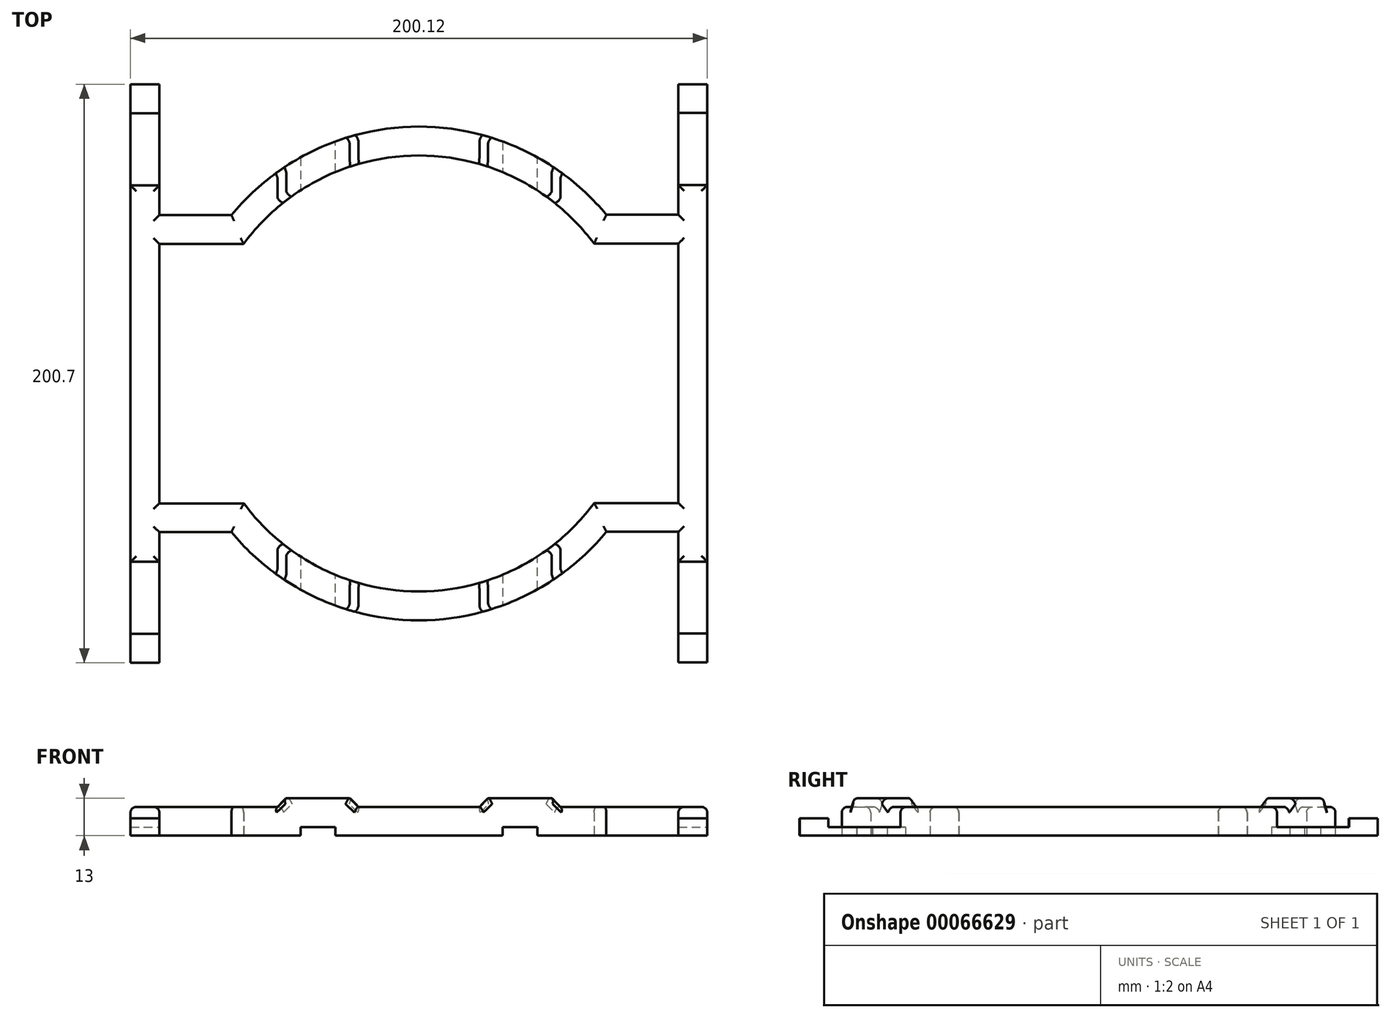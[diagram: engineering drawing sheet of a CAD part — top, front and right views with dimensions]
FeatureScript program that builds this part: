
annotation { "Feature Type Name" : "Feature", "Feature Type Description" : "" }
export const myFeature = defineFeature(function(context is Context, id is Id, definition is map)
    precondition{}
    {
        {
            var Q0;
            Q0=qCreatedBy(makeId("Top.planeOp"),FACE);
            var sketch = newSketch(context, id + "F0", { "sketchPlane" : qUnion([Q0])});
            skArc(sketch, "E0", {"start": v(-60.76, -45.05) * mm, "mid": v(0.06, -75.64) * mm, "end": v(60.83, -44.95) * mm});
            skLineSegment(sketch, "E1.bottom", {"start": v(-100.07, 100.25) * mm, "end": v(-90.07, 100.25) * mm});
            skLineSegment(sketch, "E1.top", {"start": v(-100.07, -100.35) * mm, "end": v(-90.07, -100.35) * mm});
            skLineSegment(sketch, "E2.bottom", {"start": v(90.05, 100.35) * mm, "end": v(100.05, 100.35) * mm});
            skLineSegment(sketch, "E2.top", {"start": v(90.05, -100.25) * mm, "end": v(100.05, -100.25) * mm});
            skLineSegment(sketch, "E3.bottom", {"start": v(-90.07, 54.95) * mm, "end": v(-65.07, 54.95) * mm});
            skLineSegment(sketch, "E4.bottom", {"start": v(-90.07, -55.05) * mm, "end": v(-65.07, -55.05) * mm});
            skLineSegment(sketch, "E5.bottom", {"start": v(90.05, 55.05) * mm, "end": v(65.05, 55.05) * mm});
            skLineSegment(sketch, "E6.top", {"start": v(90.05, -54.95) * mm, "end": v(65.05, -54.95) * mm});
            skLineSegment(sketch, "E7", {"start": v(-19, 83.46) * mm, "end": v(-19, 73.21) * mm});
            skLineSegment(sketch, "E8", {"start": v(-29, -80.52) * mm, "end": v(-29, -69.86) * mm});
            skLineSegment(sketch, "E9", {"start": v(19, 83.48) * mm, "end": v(19, 73.21) * mm});
            skLineSegment(sketch, "E10", {"start": v(41.12, -74.92) * mm, "end": v(41.12, -63.48) * mm});
            skLineSegment(sketch, "E11", {"start": v(-41.05, 74.96) * mm, "end": v(-41.05, 63.53) * mm});
            skLineSegment(sketch, "E12", {"start": v(-51.05, 68.42) * mm, "end": v(-51.05, 55.81) * mm});
            skLineSegment(sketch, "E13", {"start": v(51.12, -68.36) * mm, "end": v(51.12, -55.75) * mm});
            skLineSegment(sketch, "E14", {"start": v(29.07, 80.49) * mm, "end": v(29.07, 69.83) * mm});
            skLineSegment(sketch, "E15.trimOffspring", {"start": v(90.05, 45.05) * mm, "end": v(90.05, -44.95) * mm});
            skLineSegment(sketch, "E16.trimOffspring", {"start": v(-90.07, 44.95) * mm, "end": v(-90.07, -45.05) * mm});
            skLineSegment(sketch, "E17.trimOffspring", {"start": v(-51.05, -55.81) * mm, "end": v(-51.05, -68.48) * mm});
            skLineSegment(sketch, "E18.trimOffspring", {"start": v(-41.05, -63.53) * mm, "end": v(-41.05, -75) * mm});
            skLineSegment(sketch, "E19.trimOffspring", {"start": v(-29, 69.86) * mm, "end": v(-29, 80.48) * mm});
            skLineSegment(sketch, "E20.trimOffspring", {"start": v(-19, -73.21) * mm, "end": v(-19, -83.48) * mm});
            skLineSegment(sketch, "E21.trimOffspring", {"start": v(19, -73.21) * mm, "end": v(19, -83.46) * mm});
            skLineSegment(sketch, "E22.trimOffspring", {"start": v(29.07, -69.83) * mm, "end": v(29.07, -80.46) * mm});
            skLineSegment(sketch, "E23.trimOffspring", {"start": v(41.12, 63.48) * mm, "end": v(41.12, 74.96) * mm});
            skLineSegment(sketch, "E24.trimOffspring", {"start": v(51.12, 55.75) * mm, "end": v(51.12, 68.42) * mm});
            skArc(sketch, "E25.trimOffspring", {"start": v(-65.07, -55.05) * mm, "mid": v(0.02, -85.64) * mm, "end": v(65.05, -54.95) * mm});
            skArc(sketch, "E26.trimOffspring", {"start": v(65.05, 55.05) * mm, "mid": v(-0.03, 85.64) * mm, "end": v(-65.07, 54.95) * mm});
            skArc(sketch, "E27.trimOffspring", {"start": v(60.76, 45.05) * mm, "mid": v(-0.06, 75.64) * mm, "end": v(-60.83, 44.95) * mm});
            skLineSegment(sketch, "E28", {"start": v(-90.07, 44.95) * mm, "end": v(-60.83, 44.95) * mm});
            skLineSegment(sketch, "E29", {"start": v(-90.07, -45.05) * mm, "end": v(-60.76, -45.05) * mm});
            skLineSegment(sketch, "E30", {"start": v(60.83, -44.95) * mm, "end": v(90.05, -44.95) * mm});
            skLineSegment(sketch, "E31", {"start": v(90.05, 45.05) * mm, "end": v(60.76, 45.05) * mm});
            skLineSegment(sketch, "E32.bottom", {"start": v(-100.07, 65.25) * mm, "end": v(-90.07, 65.25) * mm});
            skLineSegment(sketch, "E32.top", {"start": v(-100.07, 90.25) * mm, "end": v(-90.07, 90.25) * mm});
            skLineSegment(sketch, "E32.left", {"start": v(-100.07, 65.25) * mm, "end": v(-100.07, 90.25) * mm});
            skLineSegment(sketch, "E33.bottom", {"start": v(-100.07, -90.35) * mm, "end": v(-90.07, -90.35) * mm});
            skLineSegment(sketch, "E33.top", {"start": v(-100.07, -65.35) * mm, "end": v(-90.07, -65.35) * mm});
            skLineSegment(sketch, "E33.left", {"start": v(-100.07, -90.35) * mm, "end": v(-100.07, -65.35) * mm});
            skLineSegment(sketch, "E33.right", {"start": v(-90.07, -90.35) * mm, "end": v(-90.07, -65.35) * mm});
            skLineSegment(sketch, "E34.bottom", {"start": v(90.05, -90.25) * mm, "end": v(100.05, -90.25) * mm});
            skLineSegment(sketch, "E34.top", {"start": v(90.05, -65.25) * mm, "end": v(100.05, -65.25) * mm});
            skLineSegment(sketch, "E34.left", {"start": v(90.05, -90.25) * mm, "end": v(90.05, -65.25) * mm});
            skLineSegment(sketch, "E34.right", {"start": v(100.05, -90.25) * mm, "end": v(100.05, -65.25) * mm});
            skLineSegment(sketch, "E35.bottom", {"start": v(90.05, 65.35) * mm, "end": v(100.05, 65.35) * mm});
            skLineSegment(sketch, "E35.top", {"start": v(90.05, 90.35) * mm, "end": v(100.05, 90.35) * mm});
            skLineSegment(sketch, "E35.left", {"start": v(90.05, 65.35) * mm, "end": v(90.05, 90.35) * mm});
            skLineSegment(sketch, "E35.right", {"start": v(100.05, 65.35) * mm, "end": v(100.05, 90.35) * mm});
            skLineSegment(sketch, "E36", {"start": v(-100.07, 90.25) * mm, "end": v(-100.07, 100.25) * mm});
            skLineSegment(sketch, "E37", {"start": v(-90.07, 100.25) * mm, "end": v(-90.07, 90.25) * mm});
            skLineSegment(sketch, "E38", {"start": v(-90.07, -65.35) * mm, "end": v(-90.07, -55.05) * mm});
            skLineSegment(sketch, "E39", {"start": v(-100.07, -65.35) * mm, "end": v(-100.07, 65.25) * mm});
            skLineSegment(sketch, "E40", {"start": v(-100.07, -90.35) * mm, "end": v(-100.07, -100.35) * mm});
            skLineSegment(sketch, "E41", {"start": v(-90.07, -100.35) * mm, "end": v(-90.07, -90.35) * mm});
            skLineSegment(sketch, "E42", {"start": v(90.05, -100.25) * mm, "end": v(90.05, -90.25) * mm});
            skLineSegment(sketch, "E43", {"start": v(90.05, -65.25) * mm, "end": v(90.05, -54.95) * mm});
            skLineSegment(sketch, "E44", {"start": v(100.05, -65.25) * mm, "end": v(100.05, 65.35) * mm});
            skLineSegment(sketch, "E45", {"start": v(100.05, 90.35) * mm, "end": v(100.05, 100.35) * mm});
            skLineSegment(sketch, "E46", {"start": v(90.05, 100.35) * mm, "end": v(90.05, 90.35) * mm});
            skLineSegment(sketch, "E47", {"start": v(90.05, 65.35) * mm, "end": v(90.05, 55.05) * mm});
            skLineSegment(sketch, "E48", {"start": v(100.05, -90.25) * mm, "end": v(100.05, -100.25) * mm});
            skLineSegment(sketch, "E49", {"start": v(-90.07, 90.25) * mm, "end": v(-90.07, 65.25) * mm});
            skLineSegment(sketch, "E50", {"start": v(-90.07, 54.95) * mm, "end": v(-90.07, 65.25) * mm});
            skLineSegment(sketch, "E51", {"start": v(0, 75.64) * mm, "end": v(0, 85.64) * mm});
            skLineSegment(sketch, "E52", {"start": v(0.06, -75.64) * mm, "end": v(0.06, -85.64) * mm});
            skPoint(sketch, "E52.startSnap0", {"position": v(0.06, -75.64) * mm});
            skLineSegment(sketch, "E53", {"start": v(-90.07, 44.95) * mm, "end": v(-90.07, 54.95) * mm});
            skSolve(sketch);
        }
        {
            var Q0;
            Q0=makeQuery(id+"F0.imprint","IMPRINT",FACE,{"disambiguationData":[TD([[makeQuery(id+"F0.imprint","IMPRINT",EDGE,{"derivedFrom":sQuery(id+"F0.wireOp",EDGE,"E1.bottom")}),-1.0]])]});
            var Q1;
            {var subQ0=sQuery(id+"F0.wireOp",EDGE,"E11");Q1=makeQuery(id+"F0.imprint","IMPRINT",FACE,{"disambiguationData":[TD([[makeQuery(id+"F0.imprint","IMPRINT",EDGE,{"derivedFrom":subQ0}),-1.0]])]});}
            var Q2;
            {var subQ0=sQuery(id+"F0.wireOp",EDGE,"E7");Q2=makeQuery(id+"F0.imprint","IMPRINT",FACE,{"disambiguationData":[TD([[makeQuery(id+"F0.imprint","IMPRINT",EDGE,{"derivedFrom":subQ0}),-1.0]])]});}
            var Q3;
            {var subQ0=sQuery(id+"F0.wireOp",EDGE,"E11");Q3=makeQuery(id+"F0.imprint","IMPRINT",FACE,{"disambiguationData":[TD([[makeQuery(id+"F0.imprint","IMPRINT",EDGE,{"derivedFrom":subQ0}),1.0]])]});}
            var Q4;
            {var subQ0=sQuery(id+"F0.wireOp",EDGE,"E7");Q4=makeQuery(id+"F0.imprint","IMPRINT",FACE,{"disambiguationData":[TD([[makeQuery(id+"F0.imprint","IMPRINT",EDGE,{"derivedFrom":subQ0}),1.0]])]});}
            var Q5;
            {var subQ0=sQuery(id+"F0.wireOp",EDGE,"E9");Q5=makeQuery(id+"F0.imprint","IMPRINT",FACE,{"disambiguationData":[TD([[makeQuery(id+"F0.imprint","IMPRINT",EDGE,{"derivedFrom":subQ0}),1.0]])]});}
            var Q6;
            {var subQ0=sQuery(id+"F0.wireOp",EDGE,"E14");Q6=makeQuery(id+"F0.imprint","IMPRINT",FACE,{"disambiguationData":[TD([[makeQuery(id+"F0.imprint","IMPRINT",EDGE,{"derivedFrom":subQ0}),1.0]])]});}
            var Q7;
            Q7=makeQuery(id+"F0.imprint","IMPRINT",FACE,{"disambiguationData":[TD([[makeQuery(id+"F0.imprint","IMPRINT",EDGE,{"derivedFrom":sQuery(id+"F0.wireOp",EDGE,"E2.bottom")}),-1.0]])]});
            var Q8;
            {var subQ0=sQuery(id+"F0.wireOp",EDGE,"E23.trimOffspring");Q8=makeQuery(id+"F0.imprint","IMPRINT",FACE,{"disambiguationData":[TD([[makeQuery(id+"F0.imprint","IMPRINT",EDGE,{"derivedFrom":subQ0}),-1.0]])]});}
            var Q9;
            {var subQ0=sQuery(id+"F0.wireOp",EDGE,"E10");Q9=makeQuery(id+"F0.imprint","IMPRINT",FACE,{"disambiguationData":[TD([[makeQuery(id+"F0.imprint","IMPRINT",EDGE,{"derivedFrom":subQ0}),-1.0]])]});}
            var Q10;
            {var subQ0=sQuery(id+"F0.wireOp",EDGE,"E10");Q10=makeQuery(id+"F0.imprint","IMPRINT",FACE,{"disambiguationData":[TD([[makeQuery(id+"F0.imprint","IMPRINT",EDGE,{"derivedFrom":subQ0}),1.0]])]});}
            var Q11;
            {var subQ0=sQuery(id+"F0.wireOp",EDGE,"E21.trimOffspring");Q11=makeQuery(id+"F0.imprint","IMPRINT",FACE,{"disambiguationData":[TD([[makeQuery(id+"F0.imprint","IMPRINT",EDGE,{"derivedFrom":subQ0}),1.0]])]});}
            var Q12;
            {var subQ0=sQuery(id+"F0.wireOp",EDGE,"E20.trimOffspring");Q12=makeQuery(id+"F0.imprint","IMPRINT",FACE,{"disambiguationData":[TD([[makeQuery(id+"F0.imprint","IMPRINT",EDGE,{"derivedFrom":subQ0}),1.0]])]});}
            var Q13;
            {var subQ0=sQuery(id+"F0.wireOp",EDGE,"E8");Q13=makeQuery(id+"F0.imprint","IMPRINT",FACE,{"disambiguationData":[TD([[makeQuery(id+"F0.imprint","IMPRINT",EDGE,{"derivedFrom":subQ0}),-1.0]])]});}
            var Q14;
            {var subQ0=sQuery(id+"F0.wireOp",EDGE,"E8");Q14=makeQuery(id+"F0.imprint","IMPRINT",FACE,{"disambiguationData":[TD([[makeQuery(id+"F0.imprint","IMPRINT",EDGE,{"derivedFrom":subQ0}),1.0]])]});}
            var Q15;
            {var subQ0=sQuery(id+"F0.wireOp",EDGE,"E17.trimOffspring");Q15=makeQuery(id+"F0.imprint","IMPRINT",FACE,{"disambiguationData":[TD([[makeQuery(id+"F0.imprint","IMPRINT",EDGE,{"derivedFrom":subQ0}),1.0]])]});}
            var Q16;
            Q16=makeQuery(id+"F0.imprint","IMPRINT",FACE,{"disambiguationData":[TD([[makeQuery(id+"F0.imprint","IMPRINT",EDGE,{"derivedFrom":sQuery(id+"F0.wireOp",EDGE,"E32.bottom")}),1.0]])]});
            var Q17;
            {var subQ1=sQuery(id+"F0.wireOp",EDGE,"E4.bottom");Q17=makeQuery(id+"F0.imprint","IMPRINT",FACE,{"disambiguationData":[TD([[makeQuery(id+"F0.imprint","IMPRINT",EDGE,{"derivedFrom":subQ1}),1.0]])]});}
            var Q18;
            {var subQ4=sQuery(id+"F0.wireOp",EDGE,"E3.bottom");Q18=makeQuery(id+"F0.imprint","IMPRINT",FACE,{"disambiguationData":[TD([[makeQuery(id+"F0.imprint","IMPRINT",EDGE,{"derivedFrom":subQ4}),-1.0]])]});}
            var Q19;
            {var subQ0=sQuery(id+"F0.wireOp",EDGE,"E9");Q19=makeQuery(id+"F0.imprint","IMPRINT",FACE,{"disambiguationData":[TD([[makeQuery(id+"F0.imprint","IMPRINT",EDGE,{"derivedFrom":subQ0}),-1.0]])]});}
            var Q20;
            {var subQ1=sQuery(id+"F0.wireOp",EDGE,"E5.bottom");Q20=makeQuery(id+"F0.imprint","IMPRINT",FACE,{"disambiguationData":[TD([[makeQuery(id+"F0.imprint","IMPRINT",EDGE,{"derivedFrom":subQ1}),1.0]])]});}
            var Q21;
            Q21=makeQuery(id+"F0.imprint","IMPRINT",FACE,{"disambiguationData":[TD([[makeQuery(id+"F0.imprint","IMPRINT",EDGE,{"derivedFrom":sQuery(id+"F0.wireOp",EDGE,"E35.bottom")}),1.0]])]});
            var Q22;
            Q22=makeQuery(id+"F0.imprint","IMPRINT",FACE,{"disambiguationData":[TD([[makeQuery(id+"F0.imprint","IMPRINT",EDGE,{"derivedFrom":sQuery(id+"F0.wireOp",EDGE,"E34.bottom")}),1.0]])]});
            var Q23;
            Q23=makeQuery(id+"F0.imprint","IMPRINT",FACE,{"disambiguationData":[TD([[makeQuery(id+"F0.imprint","IMPRINT",EDGE,{"derivedFrom":sQuery(id+"F0.wireOp",EDGE,"E2.top")}),1.0]])]});
            var Q24;
            {var subQ0=sQuery(id+"F0.wireOp",EDGE,"E21.trimOffspring");Q24=makeQuery(id+"F0.imprint","IMPRINT",FACE,{"disambiguationData":[TD([[makeQuery(id+"F0.imprint","IMPRINT",EDGE,{"derivedFrom":subQ0}),-1.0]])]});}
            var Q25;
            Q25=makeQuery(id+"F0.imprint","IMPRINT",FACE,{"disambiguationData":[TD([[makeQuery(id+"F0.imprint","IMPRINT",EDGE,{"derivedFrom":sQuery(id+"F0.wireOp",EDGE,"E33.bottom")}),1.0]])]});
            var Q26;
            Q26=makeQuery(id+"F0.imprint","IMPRINT",FACE,{"disambiguationData":[TD([[makeQuery(id+"F0.imprint","IMPRINT",EDGE,{"derivedFrom":sQuery(id+"F0.wireOp",EDGE,"E1.top")}),1.0]])]});
            extrude(context, id + "F1", {"entities" : qUnion([Q0, Q1, Q2, Q3, Q4, Q5, Q6, Q7, Q8, Q9, Q10, Q11, Q12, Q13, Q14, Q15, Q16, Q17, Q18, Q19, Q20, Q21, Q22, Q23, Q24, Q25, Q26]), "depth" : 10 * mm});
        }
        {
            var Q0;
            {var subQ0=sQuery(id+"F0.wireOp",EDGE,"E17.trimOffspring");Q0=makeQuery(id+"F0.imprint","IMPRINT",FACE,{"disambiguationData":[TD([[makeQuery(id+"F0.imprint","IMPRINT",EDGE,{"derivedFrom":subQ0}),1.0]])]});}
            var Q1;
            {var subQ0=sQuery(id+"F0.wireOp",EDGE,"E8");Q1=makeQuery(id+"F0.imprint","IMPRINT",FACE,{"disambiguationData":[TD([[makeQuery(id+"F0.imprint","IMPRINT",EDGE,{"derivedFrom":subQ0}),1.0]])]});}
            var Q2;
            {var subQ0=sQuery(id+"F0.wireOp",EDGE,"E8");Q2=makeQuery(id+"F0.imprint","IMPRINT",FACE,{"disambiguationData":[TD([[makeQuery(id+"F0.imprint","IMPRINT",EDGE,{"derivedFrom":subQ0}),-1.0]])]});}
            var Q3;
            {var subQ0=sQuery(id+"F0.wireOp",EDGE,"E21.trimOffspring");Q3=makeQuery(id+"F0.imprint","IMPRINT",FACE,{"disambiguationData":[TD([[makeQuery(id+"F0.imprint","IMPRINT",EDGE,{"derivedFrom":subQ0}),1.0]])]});}
            var Q4;
            {var subQ0=sQuery(id+"F0.wireOp",EDGE,"E10");Q4=makeQuery(id+"F0.imprint","IMPRINT",FACE,{"disambiguationData":[TD([[makeQuery(id+"F0.imprint","IMPRINT",EDGE,{"derivedFrom":subQ0}),1.0]])]});}
            var Q5;
            {var subQ0=sQuery(id+"F0.wireOp",EDGE,"E10");Q5=makeQuery(id+"F0.imprint","IMPRINT",FACE,{"disambiguationData":[TD([[makeQuery(id+"F0.imprint","IMPRINT",EDGE,{"derivedFrom":subQ0}),-1.0]])]});}
            var Q6;
            {var subQ0=sQuery(id+"F0.wireOp",EDGE,"E23.trimOffspring");Q6=makeQuery(id+"F0.imprint","IMPRINT",FACE,{"disambiguationData":[TD([[makeQuery(id+"F0.imprint","IMPRINT",EDGE,{"derivedFrom":subQ0}),-1.0]])]});}
            var Q7;
            {var subQ0=sQuery(id+"F0.wireOp",EDGE,"E14");Q7=makeQuery(id+"F0.imprint","IMPRINT",FACE,{"disambiguationData":[TD([[makeQuery(id+"F0.imprint","IMPRINT",EDGE,{"derivedFrom":subQ0}),1.0]])]});}
            var Q8;
            {var subQ0=sQuery(id+"F0.wireOp",EDGE,"E9");Q8=makeQuery(id+"F0.imprint","IMPRINT",FACE,{"disambiguationData":[TD([[makeQuery(id+"F0.imprint","IMPRINT",EDGE,{"derivedFrom":subQ0}),1.0]])]});}
            var Q9;
            {var subQ0=sQuery(id+"F0.wireOp",EDGE,"E7");Q9=makeQuery(id+"F0.imprint","IMPRINT",FACE,{"disambiguationData":[TD([[makeQuery(id+"F0.imprint","IMPRINT",EDGE,{"derivedFrom":subQ0}),-1.0]])]});}
            var Q10;
            {var subQ0=sQuery(id+"F0.wireOp",EDGE,"E11");Q10=makeQuery(id+"F0.imprint","IMPRINT",FACE,{"disambiguationData":[TD([[makeQuery(id+"F0.imprint","IMPRINT",EDGE,{"derivedFrom":subQ0}),1.0]])]});}
            var Q11;
            {var subQ0=sQuery(id+"F0.wireOp",EDGE,"E11");Q11=makeQuery(id+"F0.imprint","IMPRINT",FACE,{"disambiguationData":[TD([[makeQuery(id+"F0.imprint","IMPRINT",EDGE,{"derivedFrom":subQ0}),-1.0]])]});}
            extrude(context, id + "F2", {"entities" : qUnion([Q0, Q1, Q2, Q3, Q4, Q5, Q6, Q7, Q8, Q9, Q10, Q11]), "operationType" : NewBodyOperationType.ADD, "depth" : 13 * mm});
        }
        {
            var Q0;
            {var subQ0=sQuery(id+"F0.wireOp",EDGE,"E8");Q0=makeQuery(id+"F0.imprint","IMPRINT",FACE,{"disambiguationData":[TD([[makeQuery(id+"F0.imprint","IMPRINT",EDGE,{"derivedFrom":subQ0}),1.0]])]});}
            var Q1;
            {var subQ0=sQuery(id+"F0.wireOp",EDGE,"E10");Q1=makeQuery(id+"F0.imprint","IMPRINT",FACE,{"disambiguationData":[TD([[makeQuery(id+"F0.imprint","IMPRINT",EDGE,{"derivedFrom":subQ0}),1.0]])]});}
            var Q2;
            {var subQ0=sQuery(id+"F0.wireOp",EDGE,"E14");Q2=makeQuery(id+"F0.imprint","IMPRINT",FACE,{"disambiguationData":[TD([[makeQuery(id+"F0.imprint","IMPRINT",EDGE,{"derivedFrom":subQ0}),1.0]])]});}
            var Q3;
            {var subQ0=sQuery(id+"F0.wireOp",EDGE,"E11");Q3=makeQuery(id+"F0.imprint","IMPRINT",FACE,{"disambiguationData":[TD([[makeQuery(id+"F0.imprint","IMPRINT",EDGE,{"derivedFrom":subQ0}),1.0]])]});}
            extrude(context, id + "F3", {"entities" : qUnion([Q0, Q1, Q2, Q3]), "operationType" : NewBodyOperationType.REMOVE, "depth" : 3 * mm});
        }
        {
            var Q0;
            {var subQ0=sQuery(id+"F0.wireOp",EDGE,"E25.trimOffspring");var subQ7=sQuery(id+"F0.wireOp",EDGE,"E0");var subQ16=sQuery(id+"F0.wireOp",EDGE,"E1.bottom");var subQ17=sQuery(id+"F0.wireOp",EDGE,"E49");var subQ18=sQuery(id+"F0.wireOp",EDGE,"E37");var subQ19=sQuery(id+"F0.wireOp",EDGE,"E29");var subQ20=sQuery(id+"F0.wireOp",EDGE,"E3.bottom");var subQ23=sQuery(id+"F0.wireOp",EDGE,"E41");var subQ24=sQuery(id+"F0.wireOp",EDGE,"E38");var subQ25=sQuery(id+"F0.wireOp",EDGE,"E33.right");var subQ26=sQuery(id+"F0.wireOp",EDGE,"E26.trimOffspring");var subQ27=sQuery(id+"F0.wireOp",EDGE,"E1.top");var subQ28=sQuery(id+"F0.wireOp",EDGE,"E28");var subQ29=sQuery(id+"F0.wireOp",EDGE,"E4.bottom");var subQ30=sQuery(id+"F0.wireOp",EDGE,"E50");var subQ38=sQuery(id+"F0.wireOp",EDGE,"E16.trimOffspring");var subQ39=sQuery(id+"F0.wireOp",EDGE,"E40");var subQ40=sQuery(id+"F0.wireOp",EDGE,"E39");var subQ41=sQuery(id+"F0.wireOp",EDGE,"E36");var subQ42=sQuery(id+"F0.wireOp",EDGE,"E33.left");var subQ43=sQuery(id+"F0.wireOp",EDGE,"E32.left");var subQ44=sQuery(id+"F0.wireOp",EDGE,"E27.trimOffspring");Q0=makeQuery(id+"F2.boolean.opBoolean","SPLIT",FACE,{"disambiguationData":[TD([makeQuery(id+"F1.opExtrude","SWEPT_FACE",FACE,{"disambiguationData":[OSD([subQ16])]})])],"derivedFrom":makeQuery(id+"F1.opExtrude","CAP_FACE",FACE,{"disambiguationData":[OSD([subQ7,subQ16,subQ27,sQuery(id+"F0.wireOp",EDGE,"E2.bottom"),sQuery(id+"F0.wireOp",EDGE,"E2.top"),subQ20,subQ29,sQuery(id+"F0.wireOp",EDGE,"E5.bottom"),sQuery(id+"F0.wireOp",EDGE,"E6.top"),sQuery(id+"F0.wireOp",EDGE,"E15.trimOffspring"),subQ38,subQ0,subQ26,subQ44,subQ28,subQ19,sQuery(id+"F0.wireOp",EDGE,"E30"),sQuery(id+"F0.wireOp",EDGE,"E31"),subQ43,subQ42,subQ25,sQuery(id+"F0.wireOp",EDGE,"E34.left"),sQuery(id+"F0.wireOp",EDGE,"E34.right"),sQuery(id+"F0.wireOp",EDGE,"E35.left"),sQuery(id+"F0.wireOp",EDGE,"E35.right"),subQ41,subQ18,subQ24,subQ40,subQ39,subQ23,sQuery(id+"F0.wireOp",EDGE,"E42"),sQuery(id+"F0.wireOp",EDGE,"E43"),sQuery(id+"F0.wireOp",EDGE,"E44"),sQuery(id+"F0.wireOp",EDGE,"E45"),sQuery(id+"F0.wireOp",EDGE,"E46"),sQuery(id+"F0.wireOp",EDGE,"E47"),sQuery(id+"F0.wireOp",EDGE,"E48"),subQ17,subQ30])],"isStart":false})});}
            var sketch = newSketch(context, id + "F4", { "sketchPlane" : qUnion([Q0])});
            skLineSegment(sketch, "E54.top", {"start": v(-100.07, 90.25) * mm, "end": v(-90.07, 90.25) * mm});
            skLineSegment(sketch, "E54.left", {"start": v(-100.07, 65.25) * mm, "end": v(-100.07, 90.25) * mm});
            skLineSegment(sketch, "E55", {"start": v(-90.07, 90.25) * mm, "end": v(-90.07, 65.25) * mm});
            skLineSegment(sketch, "E54.bottom", {"start": v(-100.07, 65.25) * mm, "end": v(-90.07, 65.25) * mm});
            skLineSegment(sketch, "E56.right", {"start": v(-90.07, -90.35) * mm, "end": v(-90.07, -65.35) * mm});
            skLineSegment(sketch, "E56.bottom", {"start": v(-100.07, -90.35) * mm, "end": v(-90.07, -90.35) * mm});
            skLineSegment(sketch, "E56.top", {"start": v(-100.07, -65.35) * mm, "end": v(-90.07, -65.35) * mm});
            skLineSegment(sketch, "E56.left", {"start": v(-100.07, -90.35) * mm, "end": v(-100.07, -65.35) * mm});
            skLineSegment(sketch, "E57.top", {"start": v(90.05, 90.35) * mm, "end": v(100.05, 90.35) * mm});
            skLineSegment(sketch, "E57.left", {"start": v(90.05, 65.35) * mm, "end": v(90.05, 90.35) * mm});
            skLineSegment(sketch, "E57.right", {"start": v(100.05, 65.35) * mm, "end": v(100.05, 90.35) * mm});
            skLineSegment(sketch, "E57.bottom", {"start": v(90.05, 65.35) * mm, "end": v(100.05, 65.35) * mm});
            skLineSegment(sketch, "E58.left", {"start": v(90.05, -90.25) * mm, "end": v(90.05, -65.25) * mm});
            skLineSegment(sketch, "E58.right", {"start": v(100.05, -90.25) * mm, "end": v(100.05, -65.25) * mm});
            skLineSegment(sketch, "E58.bottom", {"start": v(90.05, -90.25) * mm, "end": v(100.05, -90.25) * mm});
            skLineSegment(sketch, "E58.top", {"start": v(90.05, -65.25) * mm, "end": v(100.05, -65.25) * mm});
            skSolve(sketch);
        }
        {
            var Q0;
            Q0=makeQuery(id+"F4.imprint","IMPRINT",FACE,{"disambiguationData":[TD([[makeQuery(id+"F4.imprint","IMPRINT",EDGE,{"derivedFrom":sQuery(id+"F4.wireOp",EDGE,"E54.top")}),-1.0]])]});
            var Q1;
            Q1=makeQuery(id+"F4.imprint","IMPRINT",FACE,{"disambiguationData":[TD([[makeQuery(id+"F4.imprint","IMPRINT",EDGE,{"derivedFrom":sQuery(id+"F4.wireOp",EDGE,"E56.right")}),1.0]])]});
            var Q2;
            Q2=makeQuery(id+"F4.imprint","IMPRINT",FACE,{"disambiguationData":[TD([[makeQuery(id+"F4.imprint","IMPRINT",EDGE,{"derivedFrom":sQuery(id+"F4.wireOp",EDGE,"E58.left")}),-1.0]])]});
            var Q3;
            Q3=makeQuery(id+"F4.imprint","IMPRINT",FACE,{"disambiguationData":[TD([[makeQuery(id+"F4.imprint","IMPRINT",EDGE,{"derivedFrom":sQuery(id+"F4.wireOp",EDGE,"E57.top")}),-1.0]])]});
            extrude(context, id + "F5", {"entities" : qUnion([Q0, Q1, Q2, Q3]), "operationType" : NewBodyOperationType.REMOVE, "oppositeDirection" : true, "depth" : 7 * mm});
        }
        {
            var Q0;
            {var subQ0=sQuery(id+"F0.wireOp",EDGE,"E1.bottom");var subQ1=makeQuery(id+"F1.opExtrude","SWEPT_FACE",FACE,{"disambiguationData":[OSD([subQ0])]});var subQ2=sQuery(id+"F0.wireOp",EDGE,"E40");var subQ3=sQuery(id+"F0.wireOp",EDGE,"E39");var subQ4=sQuery(id+"F0.wireOp",EDGE,"E36");var subQ5=sQuery(id+"F0.wireOp",EDGE,"E33.left");var subQ6=sQuery(id+"F0.wireOp",EDGE,"E32.left");var subQ8=sQuery(id+"F0.wireOp",EDGE,"E49");var subQ9=sQuery(id+"F0.wireOp",EDGE,"E37");var subQ11=sQuery(id+"F0.wireOp",EDGE,"E25.trimOffspring");var subQ18=sQuery(id+"F0.wireOp",EDGE,"E0");var subQ27=sQuery(id+"F0.wireOp",EDGE,"E29");var subQ28=sQuery(id+"F0.wireOp",EDGE,"E3.bottom");var subQ31=sQuery(id+"F0.wireOp",EDGE,"E41");var subQ32=sQuery(id+"F0.wireOp",EDGE,"E38");var subQ33=sQuery(id+"F0.wireOp",EDGE,"E33.right");var subQ34=sQuery(id+"F0.wireOp",EDGE,"E26.trimOffspring");var subQ35=sQuery(id+"F0.wireOp",EDGE,"E1.top");var subQ36=sQuery(id+"F0.wireOp",EDGE,"E28");var subQ37=sQuery(id+"F0.wireOp",EDGE,"E4.bottom");var subQ38=sQuery(id+"F0.wireOp",EDGE,"E50");var subQ46=sQuery(id+"F0.wireOp",EDGE,"E16.trimOffspring");var subQ47=sQuery(id+"F0.wireOp",EDGE,"E27.trimOffspring");Q0=makeQuery(id+"F5.boolean.opBoolean","SPLIT",FACE,{"disambiguationData":[TD([subQ1])],"derivedFrom":makeQuery(id+"F2.boolean.opBoolean","SPLIT",FACE,{"disambiguationData":[TD([subQ1])],"derivedFrom":makeQuery(id+"F1.opExtrude","CAP_FACE",FACE,{"disambiguationData":[OSD([subQ18,subQ0,subQ35,sQuery(id+"F0.wireOp",EDGE,"E2.bottom"),sQuery(id+"F0.wireOp",EDGE,"E2.top"),subQ28,subQ37,sQuery(id+"F0.wireOp",EDGE,"E5.bottom"),sQuery(id+"F0.wireOp",EDGE,"E6.top"),sQuery(id+"F0.wireOp",EDGE,"E15.trimOffspring"),subQ46,subQ11,subQ34,subQ47,subQ36,subQ27,sQuery(id+"F0.wireOp",EDGE,"E30"),sQuery(id+"F0.wireOp",EDGE,"E31"),subQ6,subQ5,subQ33,sQuery(id+"F0.wireOp",EDGE,"E34.left"),sQuery(id+"F0.wireOp",EDGE,"E34.right"),sQuery(id+"F0.wireOp",EDGE,"E35.left"),sQuery(id+"F0.wireOp",EDGE,"E35.right"),subQ4,subQ9,subQ32,subQ3,subQ2,subQ31,sQuery(id+"F0.wireOp",EDGE,"E42"),sQuery(id+"F0.wireOp",EDGE,"E43"),sQuery(id+"F0.wireOp",EDGE,"E44"),sQuery(id+"F0.wireOp",EDGE,"E45"),sQuery(id+"F0.wireOp",EDGE,"E46"),sQuery(id+"F0.wireOp",EDGE,"E47"),sQuery(id+"F0.wireOp",EDGE,"E48"),subQ8,subQ38])],"isStart":false})})});}
            var Q1;
            {var subQ0=sQuery(id+"F0.wireOp",EDGE,"E1.top");var subQ1=makeQuery(id+"F1.opExtrude","SWEPT_FACE",FACE,{"disambiguationData":[OSD([subQ0])]});var subQ2=sQuery(id+"F0.wireOp",EDGE,"E40");var subQ3=sQuery(id+"F0.wireOp",EDGE,"E39");var subQ4=sQuery(id+"F0.wireOp",EDGE,"E36");var subQ5=sQuery(id+"F0.wireOp",EDGE,"E33.left");var subQ6=sQuery(id+"F0.wireOp",EDGE,"E32.left");var subQ8=sQuery(id+"F0.wireOp",EDGE,"E41");var subQ9=sQuery(id+"F0.wireOp",EDGE,"E38");var subQ10=sQuery(id+"F0.wireOp",EDGE,"E33.right");var subQ12=sQuery(id+"F0.wireOp",EDGE,"E25.trimOffspring");var subQ19=sQuery(id+"F0.wireOp",EDGE,"E0");var subQ28=sQuery(id+"F0.wireOp",EDGE,"E1.bottom");var subQ29=sQuery(id+"F0.wireOp",EDGE,"E49");var subQ30=sQuery(id+"F0.wireOp",EDGE,"E37");var subQ31=sQuery(id+"F0.wireOp",EDGE,"E29");var subQ32=sQuery(id+"F0.wireOp",EDGE,"E3.bottom");var subQ35=sQuery(id+"F0.wireOp",EDGE,"E26.trimOffspring");var subQ36=sQuery(id+"F0.wireOp",EDGE,"E28");var subQ37=sQuery(id+"F0.wireOp",EDGE,"E4.bottom");var subQ38=sQuery(id+"F0.wireOp",EDGE,"E50");var subQ46=sQuery(id+"F0.wireOp",EDGE,"E16.trimOffspring");var subQ47=sQuery(id+"F0.wireOp",EDGE,"E27.trimOffspring");Q1=makeQuery(id+"F5.boolean.opBoolean","SPLIT",FACE,{"disambiguationData":[TD([subQ1])],"derivedFrom":makeQuery(id+"F2.boolean.opBoolean","SPLIT",FACE,{"disambiguationData":[TD([makeQuery(id+"F1.opExtrude","SWEPT_FACE",FACE,{"disambiguationData":[OSD([subQ28])]})])],"derivedFrom":makeQuery(id+"F1.opExtrude","CAP_FACE",FACE,{"disambiguationData":[OSD([subQ19,subQ28,subQ0,sQuery(id+"F0.wireOp",EDGE,"E2.bottom"),sQuery(id+"F0.wireOp",EDGE,"E2.top"),subQ32,subQ37,sQuery(id+"F0.wireOp",EDGE,"E5.bottom"),sQuery(id+"F0.wireOp",EDGE,"E6.top"),sQuery(id+"F0.wireOp",EDGE,"E15.trimOffspring"),subQ46,subQ12,subQ35,subQ47,subQ36,subQ31,sQuery(id+"F0.wireOp",EDGE,"E30"),sQuery(id+"F0.wireOp",EDGE,"E31"),subQ6,subQ5,subQ10,sQuery(id+"F0.wireOp",EDGE,"E34.left"),sQuery(id+"F0.wireOp",EDGE,"E34.right"),sQuery(id+"F0.wireOp",EDGE,"E35.left"),sQuery(id+"F0.wireOp",EDGE,"E35.right"),subQ4,subQ30,subQ9,subQ3,subQ2,subQ8,sQuery(id+"F0.wireOp",EDGE,"E42"),sQuery(id+"F0.wireOp",EDGE,"E43"),sQuery(id+"F0.wireOp",EDGE,"E44"),sQuery(id+"F0.wireOp",EDGE,"E45"),sQuery(id+"F0.wireOp",EDGE,"E46"),sQuery(id+"F0.wireOp",EDGE,"E47"),sQuery(id+"F0.wireOp",EDGE,"E48"),subQ29,subQ38])],"isStart":false})})});}
            var Q2;
            {var subQ0=sQuery(id+"F0.wireOp",EDGE,"E2.top");var subQ1=makeQuery(id+"F1.opExtrude","SWEPT_FACE",FACE,{"disambiguationData":[OSD([subQ0])]});var subQ2=sQuery(id+"F0.wireOp",EDGE,"E43");var subQ3=sQuery(id+"F0.wireOp",EDGE,"E42");var subQ4=sQuery(id+"F0.wireOp",EDGE,"E34.left");var subQ6=sQuery(id+"F0.wireOp",EDGE,"E48");var subQ7=sQuery(id+"F0.wireOp",EDGE,"E45");var subQ8=sQuery(id+"F0.wireOp",EDGE,"E44");var subQ9=sQuery(id+"F0.wireOp",EDGE,"E35.right");var subQ10=sQuery(id+"F0.wireOp",EDGE,"E34.right");var subQ12=sQuery(id+"F0.wireOp",EDGE,"E26.trimOffspring");var subQ20=sQuery(id+"F0.wireOp",EDGE,"E25.trimOffspring");var subQ33=sQuery(id+"F0.wireOp",EDGE,"E0");var subQ41=sQuery(id+"F0.wireOp",EDGE,"E6.top");var subQ42=sQuery(id+"F0.wireOp",EDGE,"E30");var subQ43=sQuery(id+"F0.wireOp",EDGE,"E5.bottom");var subQ46=sQuery(id+"F0.wireOp",EDGE,"E47");var subQ47=sQuery(id+"F0.wireOp",EDGE,"E46");var subQ48=sQuery(id+"F0.wireOp",EDGE,"E35.left");var subQ49=sQuery(id+"F0.wireOp",EDGE,"E2.bottom");var subQ50=sQuery(id+"F0.wireOp",EDGE,"E15.trimOffspring");var subQ51=sQuery(id+"F0.wireOp",EDGE,"E31");var subQ52=sQuery(id+"F0.wireOp",EDGE,"E27.trimOffspring");Q2=makeQuery(id+"F5.boolean.opBoolean","SPLIT",FACE,{"disambiguationData":[TD([subQ1])],"derivedFrom":makeQuery(id+"F2.boolean.opBoolean","SPLIT",FACE,{"disambiguationData":[TD([makeQuery(id+"F1.opExtrude","SWEPT_FACE",FACE,{"disambiguationData":[OSD([subQ49])]})])],"derivedFrom":makeQuery(id+"F1.opExtrude","CAP_FACE",FACE,{"disambiguationData":[OSD([subQ33,sQuery(id+"F0.wireOp",EDGE,"E1.bottom"),sQuery(id+"F0.wireOp",EDGE,"E1.top"),subQ49,subQ0,sQuery(id+"F0.wireOp",EDGE,"E3.bottom"),sQuery(id+"F0.wireOp",EDGE,"E4.bottom"),subQ43,subQ41,subQ50,sQuery(id+"F0.wireOp",EDGE,"E16.trimOffspring"),subQ20,subQ12,subQ52,sQuery(id+"F0.wireOp",EDGE,"E28"),sQuery(id+"F0.wireOp",EDGE,"E29"),subQ42,subQ51,sQuery(id+"F0.wireOp",EDGE,"E32.left"),sQuery(id+"F0.wireOp",EDGE,"E33.left"),sQuery(id+"F0.wireOp",EDGE,"E33.right"),subQ4,subQ10,subQ48,subQ9,sQuery(id+"F0.wireOp",EDGE,"E36"),sQuery(id+"F0.wireOp",EDGE,"E37"),sQuery(id+"F0.wireOp",EDGE,"E38"),sQuery(id+"F0.wireOp",EDGE,"E39"),sQuery(id+"F0.wireOp",EDGE,"E40"),sQuery(id+"F0.wireOp",EDGE,"E41"),subQ3,subQ2,subQ8,subQ7,subQ47,subQ46,subQ6,sQuery(id+"F0.wireOp",EDGE,"E49"),sQuery(id+"F0.wireOp",EDGE,"E50")])],"isStart":false})})});}
            var Q3;
            {var subQ0=sQuery(id+"F0.wireOp",EDGE,"E2.bottom");var subQ1=makeQuery(id+"F1.opExtrude","SWEPT_FACE",FACE,{"disambiguationData":[OSD([subQ0])]});var subQ2=sQuery(id+"F0.wireOp",EDGE,"E48");var subQ3=sQuery(id+"F0.wireOp",EDGE,"E45");var subQ4=sQuery(id+"F0.wireOp",EDGE,"E44");var subQ5=sQuery(id+"F0.wireOp",EDGE,"E35.right");var subQ6=sQuery(id+"F0.wireOp",EDGE,"E34.right");var subQ8=sQuery(id+"F0.wireOp",EDGE,"E47");var subQ9=sQuery(id+"F0.wireOp",EDGE,"E46");var subQ10=sQuery(id+"F0.wireOp",EDGE,"E35.left");var subQ12=sQuery(id+"F0.wireOp",EDGE,"E26.trimOffspring");var subQ20=sQuery(id+"F0.wireOp",EDGE,"E25.trimOffspring");var subQ33=sQuery(id+"F0.wireOp",EDGE,"E0");var subQ41=sQuery(id+"F0.wireOp",EDGE,"E6.top");var subQ42=sQuery(id+"F0.wireOp",EDGE,"E30");var subQ43=sQuery(id+"F0.wireOp",EDGE,"E5.bottom");var subQ46=sQuery(id+"F0.wireOp",EDGE,"E2.top");var subQ47=sQuery(id+"F0.wireOp",EDGE,"E15.trimOffspring");var subQ48=sQuery(id+"F0.wireOp",EDGE,"E31");var subQ49=sQuery(id+"F0.wireOp",EDGE,"E43");var subQ50=sQuery(id+"F0.wireOp",EDGE,"E42");var subQ51=sQuery(id+"F0.wireOp",EDGE,"E34.left");var subQ52=sQuery(id+"F0.wireOp",EDGE,"E27.trimOffspring");Q3=makeQuery(id+"F5.boolean.opBoolean","SPLIT",FACE,{"disambiguationData":[TD([subQ1])],"derivedFrom":makeQuery(id+"F2.boolean.opBoolean","SPLIT",FACE,{"disambiguationData":[TD([subQ1])],"derivedFrom":makeQuery(id+"F1.opExtrude","CAP_FACE",FACE,{"disambiguationData":[OSD([subQ33,sQuery(id+"F0.wireOp",EDGE,"E1.bottom"),sQuery(id+"F0.wireOp",EDGE,"E1.top"),subQ0,subQ46,sQuery(id+"F0.wireOp",EDGE,"E3.bottom"),sQuery(id+"F0.wireOp",EDGE,"E4.bottom"),subQ43,subQ41,subQ47,sQuery(id+"F0.wireOp",EDGE,"E16.trimOffspring"),subQ20,subQ12,subQ52,sQuery(id+"F0.wireOp",EDGE,"E28"),sQuery(id+"F0.wireOp",EDGE,"E29"),subQ42,subQ48,sQuery(id+"F0.wireOp",EDGE,"E32.left"),sQuery(id+"F0.wireOp",EDGE,"E33.left"),sQuery(id+"F0.wireOp",EDGE,"E33.right"),subQ51,subQ6,subQ10,subQ5,sQuery(id+"F0.wireOp",EDGE,"E36"),sQuery(id+"F0.wireOp",EDGE,"E37"),sQuery(id+"F0.wireOp",EDGE,"E38"),sQuery(id+"F0.wireOp",EDGE,"E39"),sQuery(id+"F0.wireOp",EDGE,"E40"),sQuery(id+"F0.wireOp",EDGE,"E41"),subQ50,subQ49,subQ4,subQ3,subQ9,subQ8,subQ2,sQuery(id+"F0.wireOp",EDGE,"E49"),sQuery(id+"F0.wireOp",EDGE,"E50")])],"isStart":false})})});}
            extrude(context, id + "F6", {"entities" : qUnion([Q0, Q1, Q2, Q3]), "operationType" : NewBodyOperationType.REMOVE, "oppositeDirection" : true, "depth" : 4 * mm});
        }
        {
            var Q0;
            Q0=makeQuery(id+"F6.boolean.opBoolean","COPY",EDGE,{"derivedFrom":makeQuery(id+"F6.opExtrude","CAP_EDGE",EDGE,{"disambiguationData":[OSD([sQuery(id+"F0.wireOp",EDGE,"E1.top")])],"isStart":false})});
            var Q1;
            Q1=makeQuery(id+"F6.boolean.opBoolean","COPY",EDGE,{"derivedFrom":makeQuery(id+"F6.opExtrude","CAP_EDGE",EDGE,{"disambiguationData":[OSD([sQuery(id+"F0.wireOp",EDGE,"E2.top")])],"isStart":false})});
            var Q2;
            Q2=makeQuery(id+"F6.boolean.opBoolean","COPY",EDGE,{"derivedFrom":makeQuery(id+"F6.opExtrude","CAP_EDGE",EDGE,{"disambiguationData":[OSD([sQuery(id+"F0.wireOp",EDGE,"E2.bottom")])],"isStart":false})});
            var Q3;
            Q3=makeQuery(id+"F6.boolean.opBoolean","COPY",EDGE,{"derivedFrom":makeQuery(id+"F6.opExtrude","CAP_EDGE",EDGE,{"disambiguationData":[OSD([sQuery(id+"F0.wireOp",EDGE,"E1.bottom")])],"isStart":false})});
            var Q4;
            Q4=makeQuery(id+"F5.boolean.opBoolean","COPY",EDGE,{"derivedFrom":makeQuery(id+"F5.opExtrude","CAP_EDGE",EDGE,{"disambiguationData":[OSD([sQuery(id+"F4.wireOp",EDGE,"E54.left")])],"isStart":false})});
            var Q5;
            Q5=makeQuery(id+"F5.boolean.opBoolean","COPY",EDGE,{"derivedFrom":makeQuery(id+"F5.opExtrude","CAP_EDGE",EDGE,{"disambiguationData":[OSD([sQuery(id+"F4.wireOp",EDGE,"E55")])],"isStart":false})});
            var Q6;
            Q6=makeQuery(id+"F5.boolean.opBoolean","COPY",EDGE,{"derivedFrom":makeQuery(id+"F5.opExtrude","CAP_EDGE",EDGE,{"disambiguationData":[OSD([sQuery(id+"F4.wireOp",EDGE,"E56.left")])],"isStart":false})});
            var Q7;
            Q7=makeQuery(id+"F5.boolean.opBoolean","COPY",EDGE,{"derivedFrom":makeQuery(id+"F5.opExtrude","CAP_EDGE",EDGE,{"disambiguationData":[OSD([sQuery(id+"F4.wireOp",EDGE,"E58.left")])],"isStart":false})});
            var Q8;
            Q8=makeQuery(id+"F5.boolean.opBoolean","COPY",EDGE,{"derivedFrom":makeQuery(id+"F5.opExtrude","CAP_EDGE",EDGE,{"disambiguationData":[OSD([sQuery(id+"F4.wireOp",EDGE,"E58.right")])],"isStart":false})});
            var Q9;
            Q9=makeQuery(id+"F5.boolean.opBoolean","COPY",EDGE,{"derivedFrom":makeQuery(id+"F5.opExtrude","CAP_EDGE",EDGE,{"disambiguationData":[OSD([sQuery(id+"F4.wireOp",EDGE,"E57.left")])],"isStart":false})});
            var Q10;
            Q10=makeQuery(id+"F5.boolean.opBoolean","COPY",EDGE,{"derivedFrom":makeQuery(id+"F5.opExtrude","CAP_EDGE",EDGE,{"disambiguationData":[OSD([sQuery(id+"F4.wireOp",EDGE,"E57.right")])],"isStart":false})});
            var Q11;
            Q11=makeQuery(id+"F6.boolean.opBoolean","COPY",EDGE,{"derivedFrom":makeQuery(id+"F6.opExtrude","CAP_EDGE",EDGE,{"disambiguationData":[OSD([sQuery(id+"F4.wireOp",EDGE,"E57.top")])],"isStart":false})});
            var Q12;
            Q12=makeQuery(id+"F6.boolean.opBoolean","COPY",EDGE,{"derivedFrom":makeQuery(id+"F6.opExtrude","CAP_EDGE",EDGE,{"disambiguationData":[OSD([sQuery(id+"F4.wireOp",EDGE,"E58.bottom")])],"isStart":false})});
            var Q13;
            Q13=makeQuery(id+"F5.boolean.opBoolean","COPY",EDGE,{"derivedFrom":makeQuery(id+"F5.opExtrude","CAP_EDGE",EDGE,{"disambiguationData":[OSD([sQuery(id+"F4.wireOp",EDGE,"E56.right")])],"isStart":false})});
            var Q14;
            Q14=makeQuery(id+"F6.boolean.opBoolean","COPY",EDGE,{"derivedFrom":makeQuery(id+"F6.opExtrude","CAP_EDGE",EDGE,{"disambiguationData":[OSD([sQuery(id+"F4.wireOp",EDGE,"E56.bottom")])],"isStart":false})});
            var Q15;
            Q15=makeQuery(id+"F6.boolean.opBoolean","COPY",EDGE,{"derivedFrom":makeQuery(id+"F6.opExtrude","CAP_EDGE",EDGE,{"disambiguationData":[OSD([sQuery(id+"F4.wireOp",EDGE,"E54.top")])],"isStart":false})});
            var Q16;
            Q16=makeQuery(id+"F6.boolean.opBoolean","COPY",EDGE,{"derivedFrom":makeQuery(id+"F6.opExtrude","CAP_EDGE",EDGE,{"disambiguationData":[OSD([sQuery(id+"F0.wireOp",EDGE,"E37"),sQuery(id+"F0.wireOp",EDGE,"E49")])],"isStart":false})});
            var Q17;
            {var subQ0=sQuery(id+"F0.wireOp",EDGE,"E40");var subQ1=sQuery(id+"F0.wireOp",EDGE,"E39");var subQ2=sQuery(id+"F0.wireOp",EDGE,"E36");var subQ3=sQuery(id+"F0.wireOp",EDGE,"E33.left");var subQ4=sQuery(id+"F0.wireOp",EDGE,"E32.left");var subQ5=sQuery(id+"F0.wireOp",EDGE,"E1.bottom");Q17=makeQuery(id+"F6.boolean.opBoolean","COPY",EDGE,{"derivedFrom":makeQuery(id+"F6.opExtrude","CAP_EDGE",EDGE,{"disambiguationData":[OSD([subQ4,subQ3,subQ2,subQ1,subQ0]),TDD([makeQuery(id+"F5.boolean.opBoolean","SPLIT",EDGE,{"disambiguationData":[TD([makeQuery(id+"F1.opExtrude","SWEPT_FACE",FACE,{"disambiguationData":[OSD([subQ5])]})])],"derivedFrom":makeQuery(id+"F1.opExtrude","CAP_EDGE",EDGE,{"disambiguationData":[OSD([subQ4,subQ3,subQ2,subQ1,subQ0])],"isStart":false})})])],"isStart":false})});}
            var Q18;
            {var subQ0=sQuery(id+"F0.wireOp",EDGE,"E40");var subQ1=sQuery(id+"F0.wireOp",EDGE,"E39");var subQ2=sQuery(id+"F0.wireOp",EDGE,"E36");var subQ3=sQuery(id+"F0.wireOp",EDGE,"E33.left");var subQ4=sQuery(id+"F0.wireOp",EDGE,"E32.left");Q18=makeQuery(id+"F5.boolean.opBoolean","SPLIT",EDGE,{"disambiguationData":[TD([makeQuery(id+"F5.opExtrude","SWEPT_FACE",FACE,{"disambiguationData":[OSD([sQuery(id+"F4.wireOp",EDGE,"E54.bottom")])]})])],"derivedFrom":makeQuery(id+"F1.opExtrude","CAP_EDGE",EDGE,{"disambiguationData":[OSD([subQ4,subQ3,subQ2,subQ1,subQ0])],"isStart":false})});}
            var Q19;
            Q19=makeQuery(id+"F5.boolean.opBoolean","COPY",EDGE,{"derivedFrom":makeQuery(id+"F5.opExtrude","CAP_EDGE",EDGE,{"disambiguationData":[OSD([sQuery(id+"F4.wireOp",EDGE,"E56.top")])],"isStart":true})});
            var Q20;
            Q20=makeQuery(id+"F5.boolean.opBoolean","COPY",EDGE,{"derivedFrom":makeQuery(id+"F5.opExtrude","CAP_EDGE",EDGE,{"disambiguationData":[OSD([sQuery(id+"F4.wireOp",EDGE,"E54.bottom")])],"isStart":true})});
            var Q21;
            {var subQ0=sQuery(id+"F0.wireOp",EDGE,"E41");var subQ1=sQuery(id+"F0.wireOp",EDGE,"E38");var subQ2=sQuery(id+"F0.wireOp",EDGE,"E33.right");var subQ3=sQuery(id+"F0.wireOp",EDGE,"E4.bottom");Q21=makeQuery(id+"F5.boolean.opBoolean","SPLIT",EDGE,{"disambiguationData":[TD([makeQuery(id+"F1.opExtrude","SWEPT_FACE",FACE,{"disambiguationData":[OSD([subQ3])]})])],"derivedFrom":makeQuery(id+"F1.opExtrude","CAP_EDGE",EDGE,{"disambiguationData":[OSD([subQ2,subQ1,subQ0])],"isStart":false})});}
            var Q22;
            Q22=makeQuery(id+"F1.opExtrude","CAP_EDGE",EDGE,{"disambiguationData":[OSD([sQuery(id+"F0.wireOp",EDGE,"E16.trimOffspring")])],"isStart":false});
            var Q23;
            Q23=makeQuery(id+"F5.boolean.opBoolean","COPY",EDGE,{"derivedFrom":makeQuery(id+"F5.opExtrude","CAP_EDGE",EDGE,{"disambiguationData":[OSD([sQuery(id+"F4.wireOp",EDGE,"E58.top")])],"isStart":true})});
            var Q24;
            {var subQ0=sQuery(id+"F0.wireOp",EDGE,"E48");var subQ1=sQuery(id+"F0.wireOp",EDGE,"E45");var subQ2=sQuery(id+"F0.wireOp",EDGE,"E44");var subQ3=sQuery(id+"F0.wireOp",EDGE,"E35.right");var subQ4=sQuery(id+"F0.wireOp",EDGE,"E34.right");Q24=makeQuery(id+"F5.boolean.opBoolean","SPLIT",EDGE,{"disambiguationData":[TD([makeQuery(id+"F5.opExtrude","SWEPT_FACE",FACE,{"disambiguationData":[OSD([sQuery(id+"F4.wireOp",EDGE,"E57.bottom")])]})])],"derivedFrom":makeQuery(id+"F1.opExtrude","CAP_EDGE",EDGE,{"disambiguationData":[OSD([subQ4,subQ3,subQ2,subQ1,subQ0])],"isStart":false})});}
            var Q25;
            {var subQ0=sQuery(id+"F0.wireOp",EDGE,"E43");var subQ1=sQuery(id+"F0.wireOp",EDGE,"E42");var subQ2=sQuery(id+"F0.wireOp",EDGE,"E34.left");var subQ3=sQuery(id+"F0.wireOp",EDGE,"E6.top");Q25=makeQuery(id+"F5.boolean.opBoolean","SPLIT",EDGE,{"disambiguationData":[TD([makeQuery(id+"F1.opExtrude","SWEPT_FACE",FACE,{"disambiguationData":[OSD([subQ3])]})])],"derivedFrom":makeQuery(id+"F1.opExtrude","CAP_EDGE",EDGE,{"disambiguationData":[OSD([subQ2,subQ1,subQ0])],"isStart":false})});}
            var Q26;
            Q26=makeQuery(id+"F1.opExtrude","CAP_EDGE",EDGE,{"disambiguationData":[OSD([sQuery(id+"F0.wireOp",EDGE,"E15.trimOffspring")])],"isStart":false});
            var Q27;
            Q27=makeQuery(id+"F1.opExtrude","CAP_EDGE",EDGE,{"disambiguationData":[OSD([sQuery(id+"F0.wireOp",EDGE,"E50")])],"isStart":false});
            var Q28;
            {var subQ0=sQuery(id+"F0.wireOp",EDGE,"E47");var subQ1=sQuery(id+"F0.wireOp",EDGE,"E46");var subQ2=sQuery(id+"F0.wireOp",EDGE,"E35.left");var subQ3=sQuery(id+"F0.wireOp",EDGE,"E5.bottom");Q28=makeQuery(id+"F5.boolean.opBoolean","SPLIT",EDGE,{"disambiguationData":[TD([makeQuery(id+"F1.opExtrude","SWEPT_FACE",FACE,{"disambiguationData":[OSD([subQ3])]})])],"derivedFrom":makeQuery(id+"F1.opExtrude","CAP_EDGE",EDGE,{"disambiguationData":[OSD([subQ2,subQ1,subQ0])],"isStart":false})});}
            var Q29;
            Q29=makeQuery(id+"F5.boolean.opBoolean","COPY",EDGE,{"derivedFrom":makeQuery(id+"F5.opExtrude","CAP_EDGE",EDGE,{"disambiguationData":[OSD([sQuery(id+"F4.wireOp",EDGE,"E57.bottom")])],"isStart":true})});
            var Q30;
            {var subQ0=sQuery(id+"F0.wireOp",EDGE,"E48");var subQ1=sQuery(id+"F0.wireOp",EDGE,"E45");var subQ2=sQuery(id+"F0.wireOp",EDGE,"E44");var subQ3=sQuery(id+"F0.wireOp",EDGE,"E35.right");var subQ4=sQuery(id+"F0.wireOp",EDGE,"E34.right");var subQ5=sQuery(id+"F0.wireOp",EDGE,"E2.bottom");Q30=makeQuery(id+"F6.boolean.opBoolean","COPY",EDGE,{"derivedFrom":makeQuery(id+"F6.opExtrude","CAP_EDGE",EDGE,{"disambiguationData":[OSD([subQ4,subQ3,subQ2,subQ1,subQ0]),TDD([makeQuery(id+"F5.boolean.opBoolean","SPLIT",EDGE,{"disambiguationData":[TD([makeQuery(id+"F1.opExtrude","SWEPT_FACE",FACE,{"disambiguationData":[OSD([subQ5])]})])],"derivedFrom":makeQuery(id+"F1.opExtrude","CAP_EDGE",EDGE,{"disambiguationData":[OSD([subQ4,subQ3,subQ2,subQ1,subQ0])],"isStart":false})})])],"isStart":false})});}
            var Q31;
            Q31=makeQuery(id+"F6.boolean.opBoolean","COPY",EDGE,{"derivedFrom":makeQuery(id+"F6.opExtrude","CAP_EDGE",EDGE,{"disambiguationData":[OSD([sQuery(id+"F0.wireOp",EDGE,"E35.left"),sQuery(id+"F0.wireOp",EDGE,"E46"),sQuery(id+"F0.wireOp",EDGE,"E47")])],"isStart":false})});
            var Q32;
            {var subQ0=sQuery(id+"F0.wireOp",EDGE,"E48");var subQ1=sQuery(id+"F0.wireOp",EDGE,"E45");var subQ2=sQuery(id+"F0.wireOp",EDGE,"E44");var subQ3=sQuery(id+"F0.wireOp",EDGE,"E35.right");var subQ4=sQuery(id+"F0.wireOp",EDGE,"E34.right");var subQ5=sQuery(id+"F0.wireOp",EDGE,"E2.top");Q32=makeQuery(id+"F6.boolean.opBoolean","COPY",EDGE,{"derivedFrom":makeQuery(id+"F6.opExtrude","CAP_EDGE",EDGE,{"disambiguationData":[OSD([subQ4,subQ3,subQ2,subQ1,subQ0]),TDD([makeQuery(id+"F5.boolean.opBoolean","SPLIT",EDGE,{"disambiguationData":[TD([makeQuery(id+"F1.opExtrude","SWEPT_FACE",FACE,{"disambiguationData":[OSD([subQ5])]})])],"derivedFrom":makeQuery(id+"F1.opExtrude","CAP_EDGE",EDGE,{"disambiguationData":[OSD([subQ4,subQ3,subQ2,subQ1,subQ0])],"isStart":false})})])],"isStart":false})});}
            var Q33;
            Q33=makeQuery(id+"F6.boolean.opBoolean","COPY",EDGE,{"derivedFrom":makeQuery(id+"F6.opExtrude","CAP_EDGE",EDGE,{"disambiguationData":[OSD([sQuery(id+"F0.wireOp",EDGE,"E34.left"),sQuery(id+"F0.wireOp",EDGE,"E42"),sQuery(id+"F0.wireOp",EDGE,"E43")])],"isStart":false})});
            var Q34;
            Q34=makeQuery(id+"F6.boolean.opBoolean","COPY",EDGE,{"derivedFrom":makeQuery(id+"F6.opExtrude","CAP_EDGE",EDGE,{"disambiguationData":[OSD([sQuery(id+"F0.wireOp",EDGE,"E33.right"),sQuery(id+"F0.wireOp",EDGE,"E38"),sQuery(id+"F0.wireOp",EDGE,"E41")])],"isStart":false})});
            var Q35;
            {var subQ0=sQuery(id+"F0.wireOp",EDGE,"E40");var subQ1=sQuery(id+"F0.wireOp",EDGE,"E39");var subQ2=sQuery(id+"F0.wireOp",EDGE,"E36");var subQ3=sQuery(id+"F0.wireOp",EDGE,"E33.left");var subQ4=sQuery(id+"F0.wireOp",EDGE,"E32.left");var subQ5=sQuery(id+"F0.wireOp",EDGE,"E1.top");Q35=makeQuery(id+"F6.boolean.opBoolean","COPY",EDGE,{"derivedFrom":makeQuery(id+"F6.opExtrude","CAP_EDGE",EDGE,{"disambiguationData":[OSD([subQ4,subQ3,subQ2,subQ1,subQ0]),TDD([makeQuery(id+"F5.boolean.opBoolean","SPLIT",EDGE,{"disambiguationData":[TD([makeQuery(id+"F1.opExtrude","SWEPT_FACE",FACE,{"disambiguationData":[OSD([subQ5])]})])],"derivedFrom":makeQuery(id+"F1.opExtrude","CAP_EDGE",EDGE,{"disambiguationData":[OSD([subQ4,subQ3,subQ2,subQ1,subQ0])],"isStart":false})})])],"isStart":false})});}
            fillet(context, id + "F7", {"entities" : qUnion([Q0, Q1, Q2, Q3, Q4, Q5, Q6, Q7, Q8, Q9, Q10, Q11, Q12, Q13, Q14, Q15, Q16, Q17, Q18, Q19, Q20, Q21, Q22, Q23, Q24, Q25, Q26, Q27, Q28, Q29, Q30, Q31, Q32, Q33, Q34, Q35]), "radius" : 2 * mm, "tangentPropagation" : true, "allowEdgeOverflow" : false});
        }
        {
            var Q0;
            Q0=makeQuery(id+"F2.opExtrude","CAP_EDGE",EDGE,{"disambiguationData":[OSD([sQuery(id+"F0.wireOp",EDGE,"E13")])],"isStart":false});
            var Q1;
            Q1=makeQuery(id+"F2.opExtrude","CAP_EDGE",EDGE,{"disambiguationData":[OSD([sQuery(id+"F0.wireOp",EDGE,"E21.trimOffspring")])],"isStart":false});
            var Q2;
            Q2=makeQuery(id+"F2.opExtrude","CAP_EDGE",EDGE,{"disambiguationData":[OSD([sQuery(id+"F0.wireOp",EDGE,"E20.trimOffspring")])],"isStart":false});
            var Q3;
            Q3=makeQuery(id+"F2.opExtrude","CAP_EDGE",EDGE,{"disambiguationData":[OSD([sQuery(id+"F0.wireOp",EDGE,"E17.trimOffspring")])],"isStart":false});
            var Q4;
            Q4=makeQuery(id+"F2.opExtrude","CAP_EDGE",EDGE,{"disambiguationData":[OSD([sQuery(id+"F0.wireOp",EDGE,"E12")])],"isStart":false});
            var Q5;
            Q5=makeQuery(id+"F2.opExtrude","CAP_EDGE",EDGE,{"disambiguationData":[OSD([sQuery(id+"F0.wireOp",EDGE,"E7")])],"isStart":false});
            var Q6;
            Q6=makeQuery(id+"F2.opExtrude","CAP_EDGE",EDGE,{"disambiguationData":[OSD([sQuery(id+"F0.wireOp",EDGE,"E9")])],"isStart":false});
            var Q7;
            Q7=makeQuery(id+"F2.opExtrude","CAP_EDGE",EDGE,{"disambiguationData":[OSD([sQuery(id+"F0.wireOp",EDGE,"E24.trimOffspring")])],"isStart":false});
            chamfer(context, id + "F8", {"entities" : qUnion([Q0, Q1, Q2, Q3, Q4, Q5, Q6, Q7]), "width" : 5 * mm, "tangentPropagation" : true});
        }
        {
            var Q0;
            {var subQ0=sQuery(id+"F0.wireOp",EDGE,"E0");var subQ5=sQuery(id+"F0.wireOp",EDGE,"E20.trimOffspring");Q0=makeQuery(id+"F2.boolean.opBoolean","SPLIT",EDGE,{"disambiguationData":[TD([makeQuery(id+"F2.opExtrude","SWEPT_FACE",FACE,{"disambiguationData":[OSD([subQ5])]})])],"derivedFrom":makeQuery(id+"F1.opExtrude","CAP_EDGE",EDGE,{"disambiguationData":[OSD([subQ0])],"isStart":false})});}
            var Q1;
            {var subQ0=sQuery(id+"F0.wireOp",EDGE,"E0");var subQ1=makeQuery(id+"F0.imprint","INTERSECT",VERTEX,{"derivedFrom":[subQ0,sQuery(id+"F0.wireOp",EDGE,"E10")]});Q1=makeQuery(id+"F2.opExtrude","CAP_EDGE",EDGE,{"disambiguationData":[OSD([subQ0]),TDD([makeQuery(id+"F0.imprint","IMPRINT",EDGE,{"disambiguationData":[TD([[makeQuery(id+"F0.imprint","INTERSECT",VERTEX,{"derivedFrom":[subQ0,sQuery(id+"F0.wireOp",EDGE,"E21.trimOffspring")]}),-1.0]])],"derivedFrom":subQ0}),makeQuery(id+"F0.imprint","IMPRINT",EDGE,{"disambiguationData":[TD([[subQ1,1.0]])],"derivedFrom":subQ0}),makeQuery(id+"F0.imprint","IMPRINT",EDGE,{"disambiguationData":[TD([[subQ1,-1.0]])],"derivedFrom":subQ0})])],"isStart":false});}
            var Q2;
            {var subQ0=sQuery(id+"F0.wireOp",EDGE,"E25.trimOffspring");var subQ1=makeQuery(id+"F0.imprint","INTERSECT",VERTEX,{"derivedFrom":[sQuery(id+"F0.wireOp",EDGE,"E10"),subQ0]});Q2=makeQuery(id+"F2.opExtrude","CAP_EDGE",EDGE,{"disambiguationData":[OSD([subQ0]),TDD([makeQuery(id+"F0.imprint","IMPRINT",EDGE,{"disambiguationData":[TD([[makeQuery(id+"F0.imprint","INTERSECT",VERTEX,{"derivedFrom":[sQuery(id+"F0.wireOp",EDGE,"E21.trimOffspring"),subQ0]}),-1.0]])],"derivedFrom":subQ0}),makeQuery(id+"F0.imprint","IMPRINT",EDGE,{"disambiguationData":[TD([[subQ1,1.0]])],"derivedFrom":subQ0}),makeQuery(id+"F0.imprint","IMPRINT",EDGE,{"disambiguationData":[TD([[subQ1,-1.0]])],"derivedFrom":subQ0})])],"isStart":false});}
            var Q3;
            {var subQ0=sQuery(id+"F0.wireOp",EDGE,"E0");var subQ1=makeQuery(id+"F0.imprint","INTERSECT",VERTEX,{"derivedFrom":[subQ0,sQuery(id+"F0.wireOp",EDGE,"E8")]});Q3=makeQuery(id+"F2.opExtrude","CAP_EDGE",EDGE,{"disambiguationData":[OSD([subQ0]),TDD([makeQuery(id+"F0.imprint","IMPRINT",EDGE,{"disambiguationData":[TD([[makeQuery(id+"F0.imprint","INTERSECT",VERTEX,{"derivedFrom":[subQ0,sQuery(id+"F0.wireOp",EDGE,"E17.trimOffspring")]}),-1.0]])],"derivedFrom":subQ0}),makeQuery(id+"F0.imprint","IMPRINT",EDGE,{"disambiguationData":[TD([[subQ1,1.0]])],"derivedFrom":subQ0}),makeQuery(id+"F0.imprint","IMPRINT",EDGE,{"disambiguationData":[TD([[subQ1,-1.0]])],"derivedFrom":subQ0})])],"isStart":false});}
            var Q4;
            {var subQ0=sQuery(id+"F0.wireOp",EDGE,"E25.trimOffspring");var subQ1=makeQuery(id+"F0.imprint","INTERSECT",VERTEX,{"derivedFrom":[sQuery(id+"F0.wireOp",EDGE,"E8"),subQ0]});Q4=makeQuery(id+"F2.opExtrude","CAP_EDGE",EDGE,{"disambiguationData":[OSD([subQ0]),TDD([makeQuery(id+"F0.imprint","IMPRINT",EDGE,{"disambiguationData":[TD([[makeQuery(id+"F0.imprint","INTERSECT",VERTEX,{"derivedFrom":[sQuery(id+"F0.wireOp",EDGE,"E17.trimOffspring"),subQ0]}),-1.0]])],"derivedFrom":subQ0}),makeQuery(id+"F0.imprint","IMPRINT",EDGE,{"disambiguationData":[TD([[subQ1,1.0]])],"derivedFrom":subQ0}),makeQuery(id+"F0.imprint","IMPRINT",EDGE,{"disambiguationData":[TD([[subQ1,-1.0]])],"derivedFrom":subQ0})])],"isStart":false});}
            var Q5;
            {var subQ1=sQuery(id+"F0.wireOp",EDGE,"E20.trimOffspring");var subQ2=sQuery(id+"F0.wireOp",EDGE,"E25.trimOffspring");Q5=makeQuery(id+"F2.boolean.opBoolean","SPLIT",EDGE,{"disambiguationData":[TD([makeQuery(id+"F2.opExtrude","SWEPT_FACE",FACE,{"disambiguationData":[OSD([subQ1])]})])],"derivedFrom":makeQuery(id+"F1.opExtrude","CAP_EDGE",EDGE,{"disambiguationData":[OSD([subQ2])],"isStart":false})});}
            var Q6;
            {var subQ0=sQuery(id+"F0.wireOp",EDGE,"E0");var subQ4=sQuery(id+"F0.wireOp",EDGE,"E29");Q6=makeQuery(id+"F2.boolean.opBoolean","SPLIT",EDGE,{"disambiguationData":[TD([makeQuery(id+"F1.opExtrude","SWEPT_FACE",FACE,{"disambiguationData":[OSD([subQ4])]})])],"derivedFrom":makeQuery(id+"F1.opExtrude","CAP_EDGE",EDGE,{"disambiguationData":[OSD([subQ0])],"isStart":false})});}
            var Q7;
            {var subQ1=sQuery(id+"F0.wireOp",EDGE,"E25.trimOffspring");var subQ4=sQuery(id+"F0.wireOp",EDGE,"E4.bottom");Q7=makeQuery(id+"F2.boolean.opBoolean","SPLIT",EDGE,{"disambiguationData":[TD([makeQuery(id+"F1.opExtrude","SWEPT_FACE",FACE,{"disambiguationData":[OSD([subQ4])]})])],"derivedFrom":makeQuery(id+"F1.opExtrude","CAP_EDGE",EDGE,{"disambiguationData":[OSD([subQ1])],"isStart":false})});}
            var Q8;
            {var subQ0=sQuery(id+"F0.wireOp",EDGE,"E0");var subQ3=sQuery(id+"F0.wireOp",EDGE,"E30");Q8=makeQuery(id+"F2.boolean.opBoolean","SPLIT",EDGE,{"disambiguationData":[TD([makeQuery(id+"F1.opExtrude","SWEPT_FACE",FACE,{"disambiguationData":[OSD([subQ3])]})])],"derivedFrom":makeQuery(id+"F1.opExtrude","CAP_EDGE",EDGE,{"disambiguationData":[OSD([subQ0])],"isStart":false})});}
            var Q9;
            {var subQ1=sQuery(id+"F0.wireOp",EDGE,"E25.trimOffspring");var subQ2=sQuery(id+"F0.wireOp",EDGE,"E6.top");Q9=makeQuery(id+"F2.boolean.opBoolean","SPLIT",EDGE,{"disambiguationData":[TD([makeQuery(id+"F1.opExtrude","SWEPT_FACE",FACE,{"disambiguationData":[OSD([subQ2])]})])],"derivedFrom":makeQuery(id+"F1.opExtrude","CAP_EDGE",EDGE,{"disambiguationData":[OSD([subQ1])],"isStart":false})});}
            var Q10;
            Q10=makeQuery(id+"F1.opExtrude","CAP_EDGE",EDGE,{"disambiguationData":[OSD([sQuery(id+"F0.wireOp",EDGE,"E6.top")])],"isStart":false});
            var Q11;
            Q11=makeQuery(id+"F1.opExtrude","CAP_EDGE",EDGE,{"disambiguationData":[OSD([sQuery(id+"F0.wireOp",EDGE,"E30")])],"isStart":false});
            var Q12;
            Q12=makeQuery(id+"F1.opExtrude","CAP_EDGE",EDGE,{"disambiguationData":[OSD([sQuery(id+"F0.wireOp",EDGE,"E29")])],"isStart":false});
            var Q13;
            Q13=makeQuery(id+"F1.opExtrude","CAP_EDGE",EDGE,{"disambiguationData":[OSD([sQuery(id+"F0.wireOp",EDGE,"E4.bottom")])],"isStart":false});
            var Q14;
            {var subQ0=sQuery(id+"F0.wireOp",EDGE,"E25.trimOffspring");var subQ1=makeQuery(id+"F0.imprint","INTERSECT",VERTEX,{"derivedFrom":[sQuery(id+"F0.wireOp",EDGE,"E10"),subQ0]});var subQ3=makeQuery(id+"F0.imprint","INTERSECT",VERTEX,{"derivedFrom":[sQuery(id+"F0.wireOp",EDGE,"E8"),subQ0]});var subQ5=sQuery(id+"F0.wireOp",EDGE,"E17.trimOffspring");Q14=makeQuery(id+"F8.opChamfer","BLEND_EDGE",EDGE,{"blendedFrom":[makeQuery(id+"F2.opExtrude","CAP_EDGE",EDGE,{"disambiguationData":[OSD([subQ5])],"isStart":false}),makeQuery(id+"F2.boolean.opBoolean","MERGE",FACE,{"derivedFrom":[makeQuery(id+"F1.opExtrude","SWEPT_FACE",FACE,{"disambiguationData":[OSD([subQ0])]}),makeQuery(id+"F2.opExtrude","SWEPT_FACE",FACE,{"disambiguationData":[OSD([subQ0]),TDD([makeQuery(id+"F0.imprint","IMPRINT",EDGE,{"disambiguationData":[TD([[makeQuery(id+"F0.imprint","INTERSECT",VERTEX,{"derivedFrom":[subQ5,subQ0]}),-1.0]])],"derivedFrom":subQ0}),makeQuery(id+"F0.imprint","IMPRINT",EDGE,{"disambiguationData":[TD([[subQ3,1.0]])],"derivedFrom":subQ0}),makeQuery(id+"F0.imprint","IMPRINT",EDGE,{"disambiguationData":[TD([[subQ3,-1.0]])],"derivedFrom":subQ0})])]}),makeQuery(id+"F2.opExtrude","SWEPT_FACE",FACE,{"disambiguationData":[OSD([subQ0]),TDD([makeQuery(id+"F0.imprint","IMPRINT",EDGE,{"disambiguationData":[TD([[makeQuery(id+"F0.imprint","INTERSECT",VERTEX,{"derivedFrom":[sQuery(id+"F0.wireOp",EDGE,"E21.trimOffspring"),subQ0]}),-1.0]])],"derivedFrom":subQ0}),makeQuery(id+"F0.imprint","IMPRINT",EDGE,{"disambiguationData":[TD([[subQ1,1.0]])],"derivedFrom":subQ0}),makeQuery(id+"F0.imprint","IMPRINT",EDGE,{"disambiguationData":[TD([[subQ1,-1.0]])],"derivedFrom":subQ0})])]})]})],"blendedInto":[makeQuery(id+"F2.boolean.opBoolean","MERGE",FACE,{"derivedFrom":[makeQuery(id+"F1.opExtrude","SWEPT_FACE",FACE,{"disambiguationData":[OSD([subQ0])]}),makeQuery(id+"F2.opExtrude","SWEPT_FACE",FACE,{"disambiguationData":[OSD([subQ0]),TDD([makeQuery(id+"F0.imprint","IMPRINT",EDGE,{"disambiguationData":[TD([[makeQuery(id+"F0.imprint","INTERSECT",VERTEX,{"derivedFrom":[subQ5,subQ0]}),-1.0]])],"derivedFrom":subQ0}),makeQuery(id+"F0.imprint","IMPRINT",EDGE,{"disambiguationData":[TD([[subQ3,1.0]])],"derivedFrom":subQ0}),makeQuery(id+"F0.imprint","IMPRINT",EDGE,{"disambiguationData":[TD([[subQ3,-1.0]])],"derivedFrom":subQ0})])]}),makeQuery(id+"F2.opExtrude","SWEPT_FACE",FACE,{"disambiguationData":[OSD([subQ0]),TDD([makeQuery(id+"F0.imprint","IMPRINT",EDGE,{"disambiguationData":[TD([[makeQuery(id+"F0.imprint","INTERSECT",VERTEX,{"derivedFrom":[sQuery(id+"F0.wireOp",EDGE,"E21.trimOffspring"),subQ0]}),-1.0]])],"derivedFrom":subQ0}),makeQuery(id+"F0.imprint","IMPRINT",EDGE,{"disambiguationData":[TD([[subQ1,1.0]])],"derivedFrom":subQ0}),makeQuery(id+"F0.imprint","IMPRINT",EDGE,{"disambiguationData":[TD([[subQ1,-1.0]])],"derivedFrom":subQ0})])]})]})]});}
            var Q15;
            {var subQ0=sQuery(id+"F0.wireOp",EDGE,"E0");var subQ1=makeQuery(id+"F0.imprint","INTERSECT",VERTEX,{"derivedFrom":[subQ0,sQuery(id+"F0.wireOp",EDGE,"E10")]});var subQ3=makeQuery(id+"F0.imprint","INTERSECT",VERTEX,{"derivedFrom":[subQ0,sQuery(id+"F0.wireOp",EDGE,"E8")]});var subQ5=sQuery(id+"F0.wireOp",EDGE,"E17.trimOffspring");Q15=makeQuery(id+"F8.opChamfer","BLEND_EDGE",EDGE,{"blendedFrom":[makeQuery(id+"F2.opExtrude","CAP_EDGE",EDGE,{"disambiguationData":[OSD([subQ5])],"isStart":false}),makeQuery(id+"F2.boolean.opBoolean","MERGE",FACE,{"derivedFrom":[makeQuery(id+"F1.opExtrude","SWEPT_FACE",FACE,{"disambiguationData":[OSD([subQ0])]}),makeQuery(id+"F2.opExtrude","SWEPT_FACE",FACE,{"disambiguationData":[OSD([subQ0]),TDD([makeQuery(id+"F0.imprint","IMPRINT",EDGE,{"disambiguationData":[TD([[makeQuery(id+"F0.imprint","INTERSECT",VERTEX,{"derivedFrom":[subQ0,subQ5]}),-1.0]])],"derivedFrom":subQ0}),makeQuery(id+"F0.imprint","IMPRINT",EDGE,{"disambiguationData":[TD([[subQ3,1.0]])],"derivedFrom":subQ0}),makeQuery(id+"F0.imprint","IMPRINT",EDGE,{"disambiguationData":[TD([[subQ3,-1.0]])],"derivedFrom":subQ0})])]}),makeQuery(id+"F2.opExtrude","SWEPT_FACE",FACE,{"disambiguationData":[OSD([subQ0]),TDD([makeQuery(id+"F0.imprint","IMPRINT",EDGE,{"disambiguationData":[TD([[makeQuery(id+"F0.imprint","INTERSECT",VERTEX,{"derivedFrom":[subQ0,sQuery(id+"F0.wireOp",EDGE,"E21.trimOffspring")]}),-1.0]])],"derivedFrom":subQ0}),makeQuery(id+"F0.imprint","IMPRINT",EDGE,{"disambiguationData":[TD([[subQ1,1.0]])],"derivedFrom":subQ0}),makeQuery(id+"F0.imprint","IMPRINT",EDGE,{"disambiguationData":[TD([[subQ1,-1.0]])],"derivedFrom":subQ0})])]})]})],"blendedInto":[makeQuery(id+"F2.boolean.opBoolean","MERGE",FACE,{"derivedFrom":[makeQuery(id+"F1.opExtrude","SWEPT_FACE",FACE,{"disambiguationData":[OSD([subQ0])]}),makeQuery(id+"F2.opExtrude","SWEPT_FACE",FACE,{"disambiguationData":[OSD([subQ0]),TDD([makeQuery(id+"F0.imprint","IMPRINT",EDGE,{"disambiguationData":[TD([[makeQuery(id+"F0.imprint","INTERSECT",VERTEX,{"derivedFrom":[subQ0,subQ5]}),-1.0]])],"derivedFrom":subQ0}),makeQuery(id+"F0.imprint","IMPRINT",EDGE,{"disambiguationData":[TD([[subQ3,1.0]])],"derivedFrom":subQ0}),makeQuery(id+"F0.imprint","IMPRINT",EDGE,{"disambiguationData":[TD([[subQ3,-1.0]])],"derivedFrom":subQ0})])]}),makeQuery(id+"F2.opExtrude","SWEPT_FACE",FACE,{"disambiguationData":[OSD([subQ0]),TDD([makeQuery(id+"F0.imprint","IMPRINT",EDGE,{"disambiguationData":[TD([[makeQuery(id+"F0.imprint","INTERSECT",VERTEX,{"derivedFrom":[subQ0,sQuery(id+"F0.wireOp",EDGE,"E21.trimOffspring")]}),-1.0]])],"derivedFrom":subQ0}),makeQuery(id+"F0.imprint","IMPRINT",EDGE,{"disambiguationData":[TD([[subQ1,1.0]])],"derivedFrom":subQ0}),makeQuery(id+"F0.imprint","IMPRINT",EDGE,{"disambiguationData":[TD([[subQ1,-1.0]])],"derivedFrom":subQ0})])]})]})]});}
            var Q16;
            {var subQ0=sQuery(id+"F0.wireOp",EDGE,"E0");var subQ1=makeQuery(id+"F0.imprint","INTERSECT",VERTEX,{"derivedFrom":[subQ0,sQuery(id+"F0.wireOp",EDGE,"E10")]});var subQ2=sQuery(id+"F0.wireOp",EDGE,"E13");var subQ4=makeQuery(id+"F0.imprint","INTERSECT",VERTEX,{"derivedFrom":[subQ0,sQuery(id+"F0.wireOp",EDGE,"E8")]});Q16=makeQuery(id+"F8.opChamfer","BLEND_EDGE",EDGE,{"blendedFrom":[makeQuery(id+"F2.opExtrude","CAP_EDGE",EDGE,{"disambiguationData":[OSD([subQ2])],"isStart":false}),makeQuery(id+"F2.boolean.opBoolean","MERGE",FACE,{"derivedFrom":[makeQuery(id+"F1.opExtrude","SWEPT_FACE",FACE,{"disambiguationData":[OSD([subQ0])]}),makeQuery(id+"F2.opExtrude","SWEPT_FACE",FACE,{"disambiguationData":[OSD([subQ0]),TDD([makeQuery(id+"F0.imprint","IMPRINT",EDGE,{"disambiguationData":[TD([[makeQuery(id+"F0.imprint","INTERSECT",VERTEX,{"derivedFrom":[subQ0,sQuery(id+"F0.wireOp",EDGE,"E17.trimOffspring")]}),-1.0]])],"derivedFrom":subQ0}),makeQuery(id+"F0.imprint","IMPRINT",EDGE,{"disambiguationData":[TD([[subQ4,1.0]])],"derivedFrom":subQ0}),makeQuery(id+"F0.imprint","IMPRINT",EDGE,{"disambiguationData":[TD([[subQ4,-1.0]])],"derivedFrom":subQ0})])]}),makeQuery(id+"F2.opExtrude","SWEPT_FACE",FACE,{"disambiguationData":[OSD([subQ0]),TDD([makeQuery(id+"F0.imprint","IMPRINT",EDGE,{"disambiguationData":[TD([[makeQuery(id+"F0.imprint","INTERSECT",VERTEX,{"derivedFrom":[subQ0,sQuery(id+"F0.wireOp",EDGE,"E21.trimOffspring")]}),-1.0]])],"derivedFrom":subQ0}),makeQuery(id+"F0.imprint","IMPRINT",EDGE,{"disambiguationData":[TD([[subQ1,1.0]])],"derivedFrom":subQ0}),makeQuery(id+"F0.imprint","IMPRINT",EDGE,{"disambiguationData":[TD([[subQ1,-1.0]])],"derivedFrom":subQ0})])]})]})],"blendedInto":[makeQuery(id+"F2.boolean.opBoolean","MERGE",FACE,{"derivedFrom":[makeQuery(id+"F1.opExtrude","SWEPT_FACE",FACE,{"disambiguationData":[OSD([subQ0])]}),makeQuery(id+"F2.opExtrude","SWEPT_FACE",FACE,{"disambiguationData":[OSD([subQ0]),TDD([makeQuery(id+"F0.imprint","IMPRINT",EDGE,{"disambiguationData":[TD([[makeQuery(id+"F0.imprint","INTERSECT",VERTEX,{"derivedFrom":[subQ0,sQuery(id+"F0.wireOp",EDGE,"E17.trimOffspring")]}),-1.0]])],"derivedFrom":subQ0}),makeQuery(id+"F0.imprint","IMPRINT",EDGE,{"disambiguationData":[TD([[subQ4,1.0]])],"derivedFrom":subQ0}),makeQuery(id+"F0.imprint","IMPRINT",EDGE,{"disambiguationData":[TD([[subQ4,-1.0]])],"derivedFrom":subQ0})])]}),makeQuery(id+"F2.opExtrude","SWEPT_FACE",FACE,{"disambiguationData":[OSD([subQ0]),TDD([makeQuery(id+"F0.imprint","IMPRINT",EDGE,{"disambiguationData":[TD([[makeQuery(id+"F0.imprint","INTERSECT",VERTEX,{"derivedFrom":[subQ0,sQuery(id+"F0.wireOp",EDGE,"E21.trimOffspring")]}),-1.0]])],"derivedFrom":subQ0}),makeQuery(id+"F0.imprint","IMPRINT",EDGE,{"disambiguationData":[TD([[subQ1,1.0]])],"derivedFrom":subQ0}),makeQuery(id+"F0.imprint","IMPRINT",EDGE,{"disambiguationData":[TD([[subQ1,-1.0]])],"derivedFrom":subQ0})])]})]})]});}
            var Q17;
            {var subQ0=sQuery(id+"F0.wireOp",EDGE,"E25.trimOffspring");var subQ1=makeQuery(id+"F0.imprint","INTERSECT",VERTEX,{"derivedFrom":[sQuery(id+"F0.wireOp",EDGE,"E10"),subQ0]});var subQ3=sQuery(id+"F0.wireOp",EDGE,"E21.trimOffspring");var subQ4=makeQuery(id+"F0.imprint","INTERSECT",VERTEX,{"derivedFrom":[sQuery(id+"F0.wireOp",EDGE,"E8"),subQ0]});Q17=makeQuery(id+"F8.opChamfer","BLEND_EDGE",EDGE,{"blendedFrom":[makeQuery(id+"F2.opExtrude","CAP_EDGE",EDGE,{"disambiguationData":[OSD([subQ3])],"isStart":false}),makeQuery(id+"F2.boolean.opBoolean","MERGE",FACE,{"derivedFrom":[makeQuery(id+"F1.opExtrude","SWEPT_FACE",FACE,{"disambiguationData":[OSD([subQ0])]}),makeQuery(id+"F2.opExtrude","SWEPT_FACE",FACE,{"disambiguationData":[OSD([subQ0]),TDD([makeQuery(id+"F0.imprint","IMPRINT",EDGE,{"disambiguationData":[TD([[makeQuery(id+"F0.imprint","INTERSECT",VERTEX,{"derivedFrom":[sQuery(id+"F0.wireOp",EDGE,"E17.trimOffspring"),subQ0]}),-1.0]])],"derivedFrom":subQ0}),makeQuery(id+"F0.imprint","IMPRINT",EDGE,{"disambiguationData":[TD([[subQ4,1.0]])],"derivedFrom":subQ0}),makeQuery(id+"F0.imprint","IMPRINT",EDGE,{"disambiguationData":[TD([[subQ4,-1.0]])],"derivedFrom":subQ0})])]}),makeQuery(id+"F2.opExtrude","SWEPT_FACE",FACE,{"disambiguationData":[OSD([subQ0]),TDD([makeQuery(id+"F0.imprint","IMPRINT",EDGE,{"disambiguationData":[TD([[makeQuery(id+"F0.imprint","INTERSECT",VERTEX,{"derivedFrom":[subQ3,subQ0]}),-1.0]])],"derivedFrom":subQ0}),makeQuery(id+"F0.imprint","IMPRINT",EDGE,{"disambiguationData":[TD([[subQ1,1.0]])],"derivedFrom":subQ0}),makeQuery(id+"F0.imprint","IMPRINT",EDGE,{"disambiguationData":[TD([[subQ1,-1.0]])],"derivedFrom":subQ0})])]})]})],"blendedInto":[makeQuery(id+"F2.boolean.opBoolean","MERGE",FACE,{"derivedFrom":[makeQuery(id+"F1.opExtrude","SWEPT_FACE",FACE,{"disambiguationData":[OSD([subQ0])]}),makeQuery(id+"F2.opExtrude","SWEPT_FACE",FACE,{"disambiguationData":[OSD([subQ0]),TDD([makeQuery(id+"F0.imprint","IMPRINT",EDGE,{"disambiguationData":[TD([[makeQuery(id+"F0.imprint","INTERSECT",VERTEX,{"derivedFrom":[sQuery(id+"F0.wireOp",EDGE,"E17.trimOffspring"),subQ0]}),-1.0]])],"derivedFrom":subQ0}),makeQuery(id+"F0.imprint","IMPRINT",EDGE,{"disambiguationData":[TD([[subQ4,1.0]])],"derivedFrom":subQ0}),makeQuery(id+"F0.imprint","IMPRINT",EDGE,{"disambiguationData":[TD([[subQ4,-1.0]])],"derivedFrom":subQ0})])]}),makeQuery(id+"F2.opExtrude","SWEPT_FACE",FACE,{"disambiguationData":[OSD([subQ0]),TDD([makeQuery(id+"F0.imprint","IMPRINT",EDGE,{"disambiguationData":[TD([[makeQuery(id+"F0.imprint","INTERSECT",VERTEX,{"derivedFrom":[subQ3,subQ0]}),-1.0]])],"derivedFrom":subQ0}),makeQuery(id+"F0.imprint","IMPRINT",EDGE,{"disambiguationData":[TD([[subQ1,1.0]])],"derivedFrom":subQ0}),makeQuery(id+"F0.imprint","IMPRINT",EDGE,{"disambiguationData":[TD([[subQ1,-1.0]])],"derivedFrom":subQ0})])]})]})]});}
            var Q18;
            {var subQ0=sQuery(id+"F0.wireOp",EDGE,"E0");var subQ1=makeQuery(id+"F0.imprint","INTERSECT",VERTEX,{"derivedFrom":[subQ0,sQuery(id+"F0.wireOp",EDGE,"E10")]});var subQ3=sQuery(id+"F0.wireOp",EDGE,"E21.trimOffspring");var subQ4=makeQuery(id+"F0.imprint","INTERSECT",VERTEX,{"derivedFrom":[subQ0,sQuery(id+"F0.wireOp",EDGE,"E8")]});Q18=makeQuery(id+"F8.opChamfer","BLEND_EDGE",EDGE,{"blendedFrom":[makeQuery(id+"F2.opExtrude","CAP_EDGE",EDGE,{"disambiguationData":[OSD([subQ3])],"isStart":false}),makeQuery(id+"F2.boolean.opBoolean","MERGE",FACE,{"derivedFrom":[makeQuery(id+"F1.opExtrude","SWEPT_FACE",FACE,{"disambiguationData":[OSD([subQ0])]}),makeQuery(id+"F2.opExtrude","SWEPT_FACE",FACE,{"disambiguationData":[OSD([subQ0]),TDD([makeQuery(id+"F0.imprint","IMPRINT",EDGE,{"disambiguationData":[TD([[makeQuery(id+"F0.imprint","INTERSECT",VERTEX,{"derivedFrom":[subQ0,sQuery(id+"F0.wireOp",EDGE,"E17.trimOffspring")]}),-1.0]])],"derivedFrom":subQ0}),makeQuery(id+"F0.imprint","IMPRINT",EDGE,{"disambiguationData":[TD([[subQ4,1.0]])],"derivedFrom":subQ0}),makeQuery(id+"F0.imprint","IMPRINT",EDGE,{"disambiguationData":[TD([[subQ4,-1.0]])],"derivedFrom":subQ0})])]}),makeQuery(id+"F2.opExtrude","SWEPT_FACE",FACE,{"disambiguationData":[OSD([subQ0]),TDD([makeQuery(id+"F0.imprint","IMPRINT",EDGE,{"disambiguationData":[TD([[makeQuery(id+"F0.imprint","INTERSECT",VERTEX,{"derivedFrom":[subQ0,subQ3]}),-1.0]])],"derivedFrom":subQ0}),makeQuery(id+"F0.imprint","IMPRINT",EDGE,{"disambiguationData":[TD([[subQ1,1.0]])],"derivedFrom":subQ0}),makeQuery(id+"F0.imprint","IMPRINT",EDGE,{"disambiguationData":[TD([[subQ1,-1.0]])],"derivedFrom":subQ0})])]})]})],"blendedInto":[makeQuery(id+"F2.boolean.opBoolean","MERGE",FACE,{"derivedFrom":[makeQuery(id+"F1.opExtrude","SWEPT_FACE",FACE,{"disambiguationData":[OSD([subQ0])]}),makeQuery(id+"F2.opExtrude","SWEPT_FACE",FACE,{"disambiguationData":[OSD([subQ0]),TDD([makeQuery(id+"F0.imprint","IMPRINT",EDGE,{"disambiguationData":[TD([[makeQuery(id+"F0.imprint","INTERSECT",VERTEX,{"derivedFrom":[subQ0,sQuery(id+"F0.wireOp",EDGE,"E17.trimOffspring")]}),-1.0]])],"derivedFrom":subQ0}),makeQuery(id+"F0.imprint","IMPRINT",EDGE,{"disambiguationData":[TD([[subQ4,1.0]])],"derivedFrom":subQ0}),makeQuery(id+"F0.imprint","IMPRINT",EDGE,{"disambiguationData":[TD([[subQ4,-1.0]])],"derivedFrom":subQ0})])]}),makeQuery(id+"F2.opExtrude","SWEPT_FACE",FACE,{"disambiguationData":[OSD([subQ0]),TDD([makeQuery(id+"F0.imprint","IMPRINT",EDGE,{"disambiguationData":[TD([[makeQuery(id+"F0.imprint","INTERSECT",VERTEX,{"derivedFrom":[subQ0,subQ3]}),-1.0]])],"derivedFrom":subQ0}),makeQuery(id+"F0.imprint","IMPRINT",EDGE,{"disambiguationData":[TD([[subQ1,1.0]])],"derivedFrom":subQ0}),makeQuery(id+"F0.imprint","IMPRINT",EDGE,{"disambiguationData":[TD([[subQ1,-1.0]])],"derivedFrom":subQ0})])]})]})]});}
            var Q19;
            {var subQ0=sQuery(id+"F0.wireOp",EDGE,"E0");var subQ1=makeQuery(id+"F0.imprint","INTERSECT",VERTEX,{"derivedFrom":[subQ0,sQuery(id+"F0.wireOp",EDGE,"E10")]});var subQ3=makeQuery(id+"F0.imprint","INTERSECT",VERTEX,{"derivedFrom":[subQ0,sQuery(id+"F0.wireOp",EDGE,"E8")]});var subQ4=sQuery(id+"F0.wireOp",EDGE,"E20.trimOffspring");Q19=makeQuery(id+"F8.opChamfer","BLEND_EDGE",EDGE,{"blendedFrom":[makeQuery(id+"F2.opExtrude","CAP_EDGE",EDGE,{"disambiguationData":[OSD([subQ4])],"isStart":false}),makeQuery(id+"F2.boolean.opBoolean","MERGE",FACE,{"derivedFrom":[makeQuery(id+"F1.opExtrude","SWEPT_FACE",FACE,{"disambiguationData":[OSD([subQ0])]}),makeQuery(id+"F2.opExtrude","SWEPT_FACE",FACE,{"disambiguationData":[OSD([subQ0]),TDD([makeQuery(id+"F0.imprint","IMPRINT",EDGE,{"disambiguationData":[TD([[makeQuery(id+"F0.imprint","INTERSECT",VERTEX,{"derivedFrom":[subQ0,sQuery(id+"F0.wireOp",EDGE,"E17.trimOffspring")]}),-1.0]])],"derivedFrom":subQ0}),makeQuery(id+"F0.imprint","IMPRINT",EDGE,{"disambiguationData":[TD([[subQ3,1.0]])],"derivedFrom":subQ0}),makeQuery(id+"F0.imprint","IMPRINT",EDGE,{"disambiguationData":[TD([[subQ3,-1.0]])],"derivedFrom":subQ0})])]}),makeQuery(id+"F2.opExtrude","SWEPT_FACE",FACE,{"disambiguationData":[OSD([subQ0]),TDD([makeQuery(id+"F0.imprint","IMPRINT",EDGE,{"disambiguationData":[TD([[makeQuery(id+"F0.imprint","INTERSECT",VERTEX,{"derivedFrom":[subQ0,sQuery(id+"F0.wireOp",EDGE,"E21.trimOffspring")]}),-1.0]])],"derivedFrom":subQ0}),makeQuery(id+"F0.imprint","IMPRINT",EDGE,{"disambiguationData":[TD([[subQ1,1.0]])],"derivedFrom":subQ0}),makeQuery(id+"F0.imprint","IMPRINT",EDGE,{"disambiguationData":[TD([[subQ1,-1.0]])],"derivedFrom":subQ0})])]})]})],"blendedInto":[makeQuery(id+"F2.boolean.opBoolean","MERGE",FACE,{"derivedFrom":[makeQuery(id+"F1.opExtrude","SWEPT_FACE",FACE,{"disambiguationData":[OSD([subQ0])]}),makeQuery(id+"F2.opExtrude","SWEPT_FACE",FACE,{"disambiguationData":[OSD([subQ0]),TDD([makeQuery(id+"F0.imprint","IMPRINT",EDGE,{"disambiguationData":[TD([[makeQuery(id+"F0.imprint","INTERSECT",VERTEX,{"derivedFrom":[subQ0,sQuery(id+"F0.wireOp",EDGE,"E17.trimOffspring")]}),-1.0]])],"derivedFrom":subQ0}),makeQuery(id+"F0.imprint","IMPRINT",EDGE,{"disambiguationData":[TD([[subQ3,1.0]])],"derivedFrom":subQ0}),makeQuery(id+"F0.imprint","IMPRINT",EDGE,{"disambiguationData":[TD([[subQ3,-1.0]])],"derivedFrom":subQ0})])]}),makeQuery(id+"F2.opExtrude","SWEPT_FACE",FACE,{"disambiguationData":[OSD([subQ0]),TDD([makeQuery(id+"F0.imprint","IMPRINT",EDGE,{"disambiguationData":[TD([[makeQuery(id+"F0.imprint","INTERSECT",VERTEX,{"derivedFrom":[subQ0,sQuery(id+"F0.wireOp",EDGE,"E21.trimOffspring")]}),-1.0]])],"derivedFrom":subQ0}),makeQuery(id+"F0.imprint","IMPRINT",EDGE,{"disambiguationData":[TD([[subQ1,1.0]])],"derivedFrom":subQ0}),makeQuery(id+"F0.imprint","IMPRINT",EDGE,{"disambiguationData":[TD([[subQ1,-1.0]])],"derivedFrom":subQ0})])]})]})]});}
            var Q20;
            {var subQ0=sQuery(id+"F0.wireOp",EDGE,"E25.trimOffspring");var subQ1=makeQuery(id+"F0.imprint","INTERSECT",VERTEX,{"derivedFrom":[sQuery(id+"F0.wireOp",EDGE,"E10"),subQ0]});var subQ3=makeQuery(id+"F0.imprint","INTERSECT",VERTEX,{"derivedFrom":[sQuery(id+"F0.wireOp",EDGE,"E8"),subQ0]});var subQ4=sQuery(id+"F0.wireOp",EDGE,"E20.trimOffspring");Q20=makeQuery(id+"F8.opChamfer","BLEND_EDGE",EDGE,{"blendedFrom":[makeQuery(id+"F2.opExtrude","CAP_EDGE",EDGE,{"disambiguationData":[OSD([subQ4])],"isStart":false}),makeQuery(id+"F2.boolean.opBoolean","MERGE",FACE,{"derivedFrom":[makeQuery(id+"F1.opExtrude","SWEPT_FACE",FACE,{"disambiguationData":[OSD([subQ0])]}),makeQuery(id+"F2.opExtrude","SWEPT_FACE",FACE,{"disambiguationData":[OSD([subQ0]),TDD([makeQuery(id+"F0.imprint","IMPRINT",EDGE,{"disambiguationData":[TD([[makeQuery(id+"F0.imprint","INTERSECT",VERTEX,{"derivedFrom":[sQuery(id+"F0.wireOp",EDGE,"E17.trimOffspring"),subQ0]}),-1.0]])],"derivedFrom":subQ0}),makeQuery(id+"F0.imprint","IMPRINT",EDGE,{"disambiguationData":[TD([[subQ3,1.0]])],"derivedFrom":subQ0}),makeQuery(id+"F0.imprint","IMPRINT",EDGE,{"disambiguationData":[TD([[subQ3,-1.0]])],"derivedFrom":subQ0})])]}),makeQuery(id+"F2.opExtrude","SWEPT_FACE",FACE,{"disambiguationData":[OSD([subQ0]),TDD([makeQuery(id+"F0.imprint","IMPRINT",EDGE,{"disambiguationData":[TD([[makeQuery(id+"F0.imprint","INTERSECT",VERTEX,{"derivedFrom":[sQuery(id+"F0.wireOp",EDGE,"E21.trimOffspring"),subQ0]}),-1.0]])],"derivedFrom":subQ0}),makeQuery(id+"F0.imprint","IMPRINT",EDGE,{"disambiguationData":[TD([[subQ1,1.0]])],"derivedFrom":subQ0}),makeQuery(id+"F0.imprint","IMPRINT",EDGE,{"disambiguationData":[TD([[subQ1,-1.0]])],"derivedFrom":subQ0})])]})]})],"blendedInto":[makeQuery(id+"F2.boolean.opBoolean","MERGE",FACE,{"derivedFrom":[makeQuery(id+"F1.opExtrude","SWEPT_FACE",FACE,{"disambiguationData":[OSD([subQ0])]}),makeQuery(id+"F2.opExtrude","SWEPT_FACE",FACE,{"disambiguationData":[OSD([subQ0]),TDD([makeQuery(id+"F0.imprint","IMPRINT",EDGE,{"disambiguationData":[TD([[makeQuery(id+"F0.imprint","INTERSECT",VERTEX,{"derivedFrom":[sQuery(id+"F0.wireOp",EDGE,"E17.trimOffspring"),subQ0]}),-1.0]])],"derivedFrom":subQ0}),makeQuery(id+"F0.imprint","IMPRINT",EDGE,{"disambiguationData":[TD([[subQ3,1.0]])],"derivedFrom":subQ0}),makeQuery(id+"F0.imprint","IMPRINT",EDGE,{"disambiguationData":[TD([[subQ3,-1.0]])],"derivedFrom":subQ0})])]}),makeQuery(id+"F2.opExtrude","SWEPT_FACE",FACE,{"disambiguationData":[OSD([subQ0]),TDD([makeQuery(id+"F0.imprint","IMPRINT",EDGE,{"disambiguationData":[TD([[makeQuery(id+"F0.imprint","INTERSECT",VERTEX,{"derivedFrom":[sQuery(id+"F0.wireOp",EDGE,"E21.trimOffspring"),subQ0]}),-1.0]])],"derivedFrom":subQ0}),makeQuery(id+"F0.imprint","IMPRINT",EDGE,{"disambiguationData":[TD([[subQ1,1.0]])],"derivedFrom":subQ0}),makeQuery(id+"F0.imprint","IMPRINT",EDGE,{"disambiguationData":[TD([[subQ1,-1.0]])],"derivedFrom":subQ0})])]})]})]});}
            var Q21;
            {var subQ0=sQuery(id+"F0.wireOp",EDGE,"E25.trimOffspring");var subQ1=makeQuery(id+"F0.imprint","INTERSECT",VERTEX,{"derivedFrom":[sQuery(id+"F0.wireOp",EDGE,"E10"),subQ0]});var subQ2=sQuery(id+"F0.wireOp",EDGE,"E13");var subQ4=makeQuery(id+"F0.imprint","INTERSECT",VERTEX,{"derivedFrom":[sQuery(id+"F0.wireOp",EDGE,"E8"),subQ0]});Q21=makeQuery(id+"F8.opChamfer","BLEND_EDGE",EDGE,{"blendedFrom":[makeQuery(id+"F2.opExtrude","CAP_EDGE",EDGE,{"disambiguationData":[OSD([subQ2])],"isStart":false}),makeQuery(id+"F2.boolean.opBoolean","MERGE",FACE,{"derivedFrom":[makeQuery(id+"F1.opExtrude","SWEPT_FACE",FACE,{"disambiguationData":[OSD([subQ0])]}),makeQuery(id+"F2.opExtrude","SWEPT_FACE",FACE,{"disambiguationData":[OSD([subQ0]),TDD([makeQuery(id+"F0.imprint","IMPRINT",EDGE,{"disambiguationData":[TD([[makeQuery(id+"F0.imprint","INTERSECT",VERTEX,{"derivedFrom":[sQuery(id+"F0.wireOp",EDGE,"E17.trimOffspring"),subQ0]}),-1.0]])],"derivedFrom":subQ0}),makeQuery(id+"F0.imprint","IMPRINT",EDGE,{"disambiguationData":[TD([[subQ4,1.0]])],"derivedFrom":subQ0}),makeQuery(id+"F0.imprint","IMPRINT",EDGE,{"disambiguationData":[TD([[subQ4,-1.0]])],"derivedFrom":subQ0})])]}),makeQuery(id+"F2.opExtrude","SWEPT_FACE",FACE,{"disambiguationData":[OSD([subQ0]),TDD([makeQuery(id+"F0.imprint","IMPRINT",EDGE,{"disambiguationData":[TD([[makeQuery(id+"F0.imprint","INTERSECT",VERTEX,{"derivedFrom":[sQuery(id+"F0.wireOp",EDGE,"E21.trimOffspring"),subQ0]}),-1.0]])],"derivedFrom":subQ0}),makeQuery(id+"F0.imprint","IMPRINT",EDGE,{"disambiguationData":[TD([[subQ1,1.0]])],"derivedFrom":subQ0}),makeQuery(id+"F0.imprint","IMPRINT",EDGE,{"disambiguationData":[TD([[subQ1,-1.0]])],"derivedFrom":subQ0})])]})]})],"blendedInto":[makeQuery(id+"F2.boolean.opBoolean","MERGE",FACE,{"derivedFrom":[makeQuery(id+"F1.opExtrude","SWEPT_FACE",FACE,{"disambiguationData":[OSD([subQ0])]}),makeQuery(id+"F2.opExtrude","SWEPT_FACE",FACE,{"disambiguationData":[OSD([subQ0]),TDD([makeQuery(id+"F0.imprint","IMPRINT",EDGE,{"disambiguationData":[TD([[makeQuery(id+"F0.imprint","INTERSECT",VERTEX,{"derivedFrom":[sQuery(id+"F0.wireOp",EDGE,"E17.trimOffspring"),subQ0]}),-1.0]])],"derivedFrom":subQ0}),makeQuery(id+"F0.imprint","IMPRINT",EDGE,{"disambiguationData":[TD([[subQ4,1.0]])],"derivedFrom":subQ0}),makeQuery(id+"F0.imprint","IMPRINT",EDGE,{"disambiguationData":[TD([[subQ4,-1.0]])],"derivedFrom":subQ0})])]}),makeQuery(id+"F2.opExtrude","SWEPT_FACE",FACE,{"disambiguationData":[OSD([subQ0]),TDD([makeQuery(id+"F0.imprint","IMPRINT",EDGE,{"disambiguationData":[TD([[makeQuery(id+"F0.imprint","INTERSECT",VERTEX,{"derivedFrom":[sQuery(id+"F0.wireOp",EDGE,"E21.trimOffspring"),subQ0]}),-1.0]])],"derivedFrom":subQ0}),makeQuery(id+"F0.imprint","IMPRINT",EDGE,{"disambiguationData":[TD([[subQ1,1.0]])],"derivedFrom":subQ0}),makeQuery(id+"F0.imprint","IMPRINT",EDGE,{"disambiguationData":[TD([[subQ1,-1.0]])],"derivedFrom":subQ0})])]})]})]});}
            fillet(context, id + "F9", {"entities" : qUnion([Q0, Q1, Q2, Q3, Q4, Q5, Q6, Q7, Q8, Q9, Q10, Q11, Q12, Q13, Q14, Q15, Q16, Q17, Q18, Q19, Q20, Q21]), "radius" : 2 * mm, "tangentPropagation" : true, "allowEdgeOverflow" : false});
        }
        {
            var Q0;
            {var subQ1=sQuery(id+"F0.wireOp",EDGE,"E26.trimOffspring");var subQ4=sQuery(id+"F0.wireOp",EDGE,"E7");Q0=makeQuery(id+"F2.boolean.opBoolean","SPLIT",EDGE,{"disambiguationData":[TD([makeQuery(id+"F2.opExtrude","SWEPT_FACE",FACE,{"disambiguationData":[OSD([subQ4])]})])],"derivedFrom":makeQuery(id+"F1.opExtrude","CAP_EDGE",EDGE,{"disambiguationData":[OSD([subQ1])],"isStart":false})});}
            var Q1;
            {var subQ1=sQuery(id+"F0.wireOp",EDGE,"E27.trimOffspring");var subQ4=sQuery(id+"F0.wireOp",EDGE,"E7");Q1=makeQuery(id+"F2.boolean.opBoolean","SPLIT",EDGE,{"disambiguationData":[TD([makeQuery(id+"F2.opExtrude","SWEPT_FACE",FACE,{"disambiguationData":[OSD([subQ4])]})])],"derivedFrom":makeQuery(id+"F1.opExtrude","CAP_EDGE",EDGE,{"disambiguationData":[OSD([subQ1])],"isStart":false})});}
            var Q2;
            {var subQ0=sQuery(id+"F0.wireOp",EDGE,"E26.trimOffspring");var subQ1=makeQuery(id+"F0.imprint","INTERSECT",VERTEX,{"derivedFrom":[sQuery(id+"F0.wireOp",EDGE,"E11"),subQ0]});Q2=makeQuery(id+"F2.opExtrude","CAP_EDGE",EDGE,{"disambiguationData":[OSD([subQ0]),TDD([makeQuery(id+"F0.imprint","IMPRINT",EDGE,{"disambiguationData":[TD([[makeQuery(id+"F0.imprint","INTERSECT",VERTEX,{"derivedFrom":[sQuery(id+"F0.wireOp",EDGE,"E7"),subQ0]}),-1.0]])],"derivedFrom":subQ0}),makeQuery(id+"F0.imprint","IMPRINT",EDGE,{"disambiguationData":[TD([[subQ1,1.0]])],"derivedFrom":subQ0}),makeQuery(id+"F0.imprint","IMPRINT",EDGE,{"disambiguationData":[TD([[subQ1,-1.0]])],"derivedFrom":subQ0})])],"isStart":false});}
            var Q3;
            {var subQ0=sQuery(id+"F0.wireOp",EDGE,"E27.trimOffspring");var subQ1=makeQuery(id+"F0.imprint","INTERSECT",VERTEX,{"derivedFrom":[sQuery(id+"F0.wireOp",EDGE,"E11"),subQ0]});Q3=makeQuery(id+"F2.opExtrude","CAP_EDGE",EDGE,{"disambiguationData":[OSD([subQ0]),TDD([makeQuery(id+"F0.imprint","IMPRINT",EDGE,{"disambiguationData":[TD([[makeQuery(id+"F0.imprint","INTERSECT",VERTEX,{"derivedFrom":[sQuery(id+"F0.wireOp",EDGE,"E7"),subQ0]}),-1.0]])],"derivedFrom":subQ0}),makeQuery(id+"F0.imprint","IMPRINT",EDGE,{"disambiguationData":[TD([[subQ1,1.0]])],"derivedFrom":subQ0}),makeQuery(id+"F0.imprint","IMPRINT",EDGE,{"disambiguationData":[TD([[subQ1,-1.0]])],"derivedFrom":subQ0})])],"isStart":false});}
            var Q4;
            {var subQ0=sQuery(id+"F0.wireOp",EDGE,"E26.trimOffspring");var subQ1=makeQuery(id+"F0.imprint","INTERSECT",VERTEX,{"derivedFrom":[sQuery(id+"F0.wireOp",EDGE,"E14"),subQ0]});var subQ2=makeQuery(id+"F0.imprint","INTERSECT",VERTEX,{"derivedFrom":[sQuery(id+"F0.wireOp",EDGE,"E23.trimOffspring"),subQ0]});Q4=makeQuery(id+"F2.opExtrude","CAP_EDGE",EDGE,{"disambiguationData":[OSD([subQ0]),TDD([makeQuery(id+"F0.imprint","IMPRINT",EDGE,{"disambiguationData":[TD([[subQ2,1.0]])],"derivedFrom":subQ0}),makeQuery(id+"F0.imprint","IMPRINT",EDGE,{"disambiguationData":[TD([[subQ1,1.0]])],"derivedFrom":subQ0}),makeQuery(id+"F0.imprint","IMPRINT",EDGE,{"disambiguationData":[TD([[makeQuery(id+"F0.imprint","INTERSECT",VERTEX,{"derivedFrom":[sQuery(id+"F0.wireOp",EDGE,"E9"),subQ0]}),1.0]])],"derivedFrom":subQ0})])],"isStart":false});}
            var Q5;
            {var subQ0=sQuery(id+"F0.wireOp",EDGE,"E27.trimOffspring");var subQ1=makeQuery(id+"F0.imprint","INTERSECT",VERTEX,{"derivedFrom":[sQuery(id+"F0.wireOp",EDGE,"E14"),subQ0]});var subQ2=makeQuery(id+"F0.imprint","INTERSECT",VERTEX,{"derivedFrom":[sQuery(id+"F0.wireOp",EDGE,"E23.trimOffspring"),subQ0]});Q5=makeQuery(id+"F2.opExtrude","CAP_EDGE",EDGE,{"disambiguationData":[OSD([subQ0]),TDD([makeQuery(id+"F0.imprint","IMPRINT",EDGE,{"disambiguationData":[TD([[subQ2,1.0]])],"derivedFrom":subQ0}),makeQuery(id+"F0.imprint","IMPRINT",EDGE,{"disambiguationData":[TD([[subQ1,1.0]])],"derivedFrom":subQ0}),makeQuery(id+"F0.imprint","IMPRINT",EDGE,{"disambiguationData":[TD([[makeQuery(id+"F0.imprint","INTERSECT",VERTEX,{"derivedFrom":[sQuery(id+"F0.wireOp",EDGE,"E9"),subQ0]}),1.0]])],"derivedFrom":subQ0})])],"isStart":false});}
            var Q6;
            {var subQ1=sQuery(id+"F0.wireOp",EDGE,"E26.trimOffspring");var subQ2=sQuery(id+"F0.wireOp",EDGE,"E5.bottom");Q6=makeQuery(id+"F2.boolean.opBoolean","SPLIT",EDGE,{"disambiguationData":[TD([makeQuery(id+"F1.opExtrude","SWEPT_FACE",FACE,{"disambiguationData":[OSD([subQ2])]})])],"derivedFrom":makeQuery(id+"F1.opExtrude","CAP_EDGE",EDGE,{"disambiguationData":[OSD([subQ1])],"isStart":false})});}
            var Q7;
            {var subQ1=sQuery(id+"F0.wireOp",EDGE,"E31");var subQ2=sQuery(id+"F0.wireOp",EDGE,"E27.trimOffspring");Q7=makeQuery(id+"F2.boolean.opBoolean","SPLIT",EDGE,{"disambiguationData":[TD([makeQuery(id+"F1.opExtrude","SWEPT_FACE",FACE,{"disambiguationData":[OSD([subQ1])]})])],"derivedFrom":makeQuery(id+"F1.opExtrude","CAP_EDGE",EDGE,{"disambiguationData":[OSD([subQ2])],"isStart":false})});}
            var Q8;
            {var subQ0=sQuery(id+"F0.wireOp",EDGE,"E26.trimOffspring");var subQ1=sQuery(id+"F0.wireOp",EDGE,"E3.bottom");Q8=makeQuery(id+"F2.boolean.opBoolean","SPLIT",EDGE,{"disambiguationData":[TD([makeQuery(id+"F1.opExtrude","SWEPT_FACE",FACE,{"disambiguationData":[OSD([subQ1])]})])],"derivedFrom":makeQuery(id+"F1.opExtrude","CAP_EDGE",EDGE,{"disambiguationData":[OSD([subQ0])],"isStart":false})});}
            var Q9;
            {var subQ1=sQuery(id+"F0.wireOp",EDGE,"E28");var subQ2=sQuery(id+"F0.wireOp",EDGE,"E27.trimOffspring");Q9=makeQuery(id+"F2.boolean.opBoolean","SPLIT",EDGE,{"disambiguationData":[TD([makeQuery(id+"F1.opExtrude","SWEPT_FACE",FACE,{"disambiguationData":[OSD([subQ1])]})])],"derivedFrom":makeQuery(id+"F1.opExtrude","CAP_EDGE",EDGE,{"disambiguationData":[OSD([subQ2])],"isStart":false})});}
            var Q10;
            Q10=makeQuery(id+"F1.opExtrude","CAP_EDGE",EDGE,{"disambiguationData":[OSD([sQuery(id+"F0.wireOp",EDGE,"E3.bottom")])],"isStart":false});
            var Q11;
            Q11=makeQuery(id+"F1.opExtrude","CAP_EDGE",EDGE,{"disambiguationData":[OSD([sQuery(id+"F0.wireOp",EDGE,"E28")])],"isStart":false});
            var Q12;
            Q12=makeQuery(id+"F1.opExtrude","CAP_EDGE",EDGE,{"disambiguationData":[OSD([sQuery(id+"F0.wireOp",EDGE,"E5.bottom")])],"isStart":false});
            var Q13;
            Q13=makeQuery(id+"F1.opExtrude","CAP_EDGE",EDGE,{"disambiguationData":[OSD([sQuery(id+"F0.wireOp",EDGE,"E31")])],"isStart":false});
            var Q14;
            {var subQ0=sQuery(id+"F0.wireOp",EDGE,"E26.trimOffspring");var subQ1=makeQuery(id+"F0.imprint","INTERSECT",VERTEX,{"derivedFrom":[sQuery(id+"F0.wireOp",EDGE,"E11"),subQ0]});var subQ2=sQuery(id+"F0.wireOp",EDGE,"E12");var subQ4=makeQuery(id+"F0.imprint","INTERSECT",VERTEX,{"derivedFrom":[sQuery(id+"F0.wireOp",EDGE,"E14"),subQ0]});var subQ5=makeQuery(id+"F0.imprint","INTERSECT",VERTEX,{"derivedFrom":[sQuery(id+"F0.wireOp",EDGE,"E23.trimOffspring"),subQ0]});Q14=makeQuery(id+"F8.opChamfer","BLEND_EDGE",EDGE,{"blendedFrom":[makeQuery(id+"F2.opExtrude","CAP_EDGE",EDGE,{"disambiguationData":[OSD([subQ2])],"isStart":false}),makeQuery(id+"F2.boolean.opBoolean","MERGE",FACE,{"derivedFrom":[makeQuery(id+"F1.opExtrude","SWEPT_FACE",FACE,{"disambiguationData":[OSD([subQ0])]}),makeQuery(id+"F2.opExtrude","SWEPT_FACE",FACE,{"disambiguationData":[OSD([subQ0]),TDD([makeQuery(id+"F0.imprint","IMPRINT",EDGE,{"disambiguationData":[TD([[subQ5,1.0]])],"derivedFrom":subQ0}),makeQuery(id+"F0.imprint","IMPRINT",EDGE,{"disambiguationData":[TD([[subQ4,1.0]])],"derivedFrom":subQ0}),makeQuery(id+"F0.imprint","IMPRINT",EDGE,{"disambiguationData":[TD([[makeQuery(id+"F0.imprint","INTERSECT",VERTEX,{"derivedFrom":[sQuery(id+"F0.wireOp",EDGE,"E9"),subQ0]}),1.0]])],"derivedFrom":subQ0})])]}),makeQuery(id+"F2.opExtrude","SWEPT_FACE",FACE,{"disambiguationData":[OSD([subQ0]),TDD([makeQuery(id+"F0.imprint","IMPRINT",EDGE,{"disambiguationData":[TD([[makeQuery(id+"F0.imprint","INTERSECT",VERTEX,{"derivedFrom":[sQuery(id+"F0.wireOp",EDGE,"E7"),subQ0]}),-1.0]])],"derivedFrom":subQ0}),makeQuery(id+"F0.imprint","IMPRINT",EDGE,{"disambiguationData":[TD([[subQ1,1.0]])],"derivedFrom":subQ0}),makeQuery(id+"F0.imprint","IMPRINT",EDGE,{"disambiguationData":[TD([[subQ1,-1.0]])],"derivedFrom":subQ0})])]})]})],"blendedInto":[makeQuery(id+"F2.boolean.opBoolean","MERGE",FACE,{"derivedFrom":[makeQuery(id+"F1.opExtrude","SWEPT_FACE",FACE,{"disambiguationData":[OSD([subQ0])]}),makeQuery(id+"F2.opExtrude","SWEPT_FACE",FACE,{"disambiguationData":[OSD([subQ0]),TDD([makeQuery(id+"F0.imprint","IMPRINT",EDGE,{"disambiguationData":[TD([[subQ5,1.0]])],"derivedFrom":subQ0}),makeQuery(id+"F0.imprint","IMPRINT",EDGE,{"disambiguationData":[TD([[subQ4,1.0]])],"derivedFrom":subQ0}),makeQuery(id+"F0.imprint","IMPRINT",EDGE,{"disambiguationData":[TD([[makeQuery(id+"F0.imprint","INTERSECT",VERTEX,{"derivedFrom":[sQuery(id+"F0.wireOp",EDGE,"E9"),subQ0]}),1.0]])],"derivedFrom":subQ0})])]}),makeQuery(id+"F2.opExtrude","SWEPT_FACE",FACE,{"disambiguationData":[OSD([subQ0]),TDD([makeQuery(id+"F0.imprint","IMPRINT",EDGE,{"disambiguationData":[TD([[makeQuery(id+"F0.imprint","INTERSECT",VERTEX,{"derivedFrom":[sQuery(id+"F0.wireOp",EDGE,"E7"),subQ0]}),-1.0]])],"derivedFrom":subQ0}),makeQuery(id+"F0.imprint","IMPRINT",EDGE,{"disambiguationData":[TD([[subQ1,1.0]])],"derivedFrom":subQ0}),makeQuery(id+"F0.imprint","IMPRINT",EDGE,{"disambiguationData":[TD([[subQ1,-1.0]])],"derivedFrom":subQ0})])]})]})]});}
            var Q15;
            {var subQ0=sQuery(id+"F0.wireOp",EDGE,"E27.trimOffspring");var subQ1=makeQuery(id+"F0.imprint","INTERSECT",VERTEX,{"derivedFrom":[sQuery(id+"F0.wireOp",EDGE,"E11"),subQ0]});var subQ2=sQuery(id+"F0.wireOp",EDGE,"E12");var subQ4=makeQuery(id+"F0.imprint","INTERSECT",VERTEX,{"derivedFrom":[sQuery(id+"F0.wireOp",EDGE,"E14"),subQ0]});var subQ5=makeQuery(id+"F0.imprint","INTERSECT",VERTEX,{"derivedFrom":[sQuery(id+"F0.wireOp",EDGE,"E23.trimOffspring"),subQ0]});Q15=makeQuery(id+"F8.opChamfer","BLEND_EDGE",EDGE,{"blendedFrom":[makeQuery(id+"F2.opExtrude","CAP_EDGE",EDGE,{"disambiguationData":[OSD([subQ2])],"isStart":false}),makeQuery(id+"F2.boolean.opBoolean","MERGE",FACE,{"derivedFrom":[makeQuery(id+"F1.opExtrude","SWEPT_FACE",FACE,{"disambiguationData":[OSD([subQ0])]}),makeQuery(id+"F2.opExtrude","SWEPT_FACE",FACE,{"disambiguationData":[OSD([subQ0]),TDD([makeQuery(id+"F0.imprint","IMPRINT",EDGE,{"disambiguationData":[TD([[subQ5,1.0]])],"derivedFrom":subQ0}),makeQuery(id+"F0.imprint","IMPRINT",EDGE,{"disambiguationData":[TD([[subQ4,1.0]])],"derivedFrom":subQ0}),makeQuery(id+"F0.imprint","IMPRINT",EDGE,{"disambiguationData":[TD([[makeQuery(id+"F0.imprint","INTERSECT",VERTEX,{"derivedFrom":[sQuery(id+"F0.wireOp",EDGE,"E9"),subQ0]}),1.0]])],"derivedFrom":subQ0})])]}),makeQuery(id+"F2.opExtrude","SWEPT_FACE",FACE,{"disambiguationData":[OSD([subQ0]),TDD([makeQuery(id+"F0.imprint","IMPRINT",EDGE,{"disambiguationData":[TD([[makeQuery(id+"F0.imprint","INTERSECT",VERTEX,{"derivedFrom":[sQuery(id+"F0.wireOp",EDGE,"E7"),subQ0]}),-1.0]])],"derivedFrom":subQ0}),makeQuery(id+"F0.imprint","IMPRINT",EDGE,{"disambiguationData":[TD([[subQ1,1.0]])],"derivedFrom":subQ0}),makeQuery(id+"F0.imprint","IMPRINT",EDGE,{"disambiguationData":[TD([[subQ1,-1.0]])],"derivedFrom":subQ0})])]})]})],"blendedInto":[makeQuery(id+"F2.boolean.opBoolean","MERGE",FACE,{"derivedFrom":[makeQuery(id+"F1.opExtrude","SWEPT_FACE",FACE,{"disambiguationData":[OSD([subQ0])]}),makeQuery(id+"F2.opExtrude","SWEPT_FACE",FACE,{"disambiguationData":[OSD([subQ0]),TDD([makeQuery(id+"F0.imprint","IMPRINT",EDGE,{"disambiguationData":[TD([[subQ5,1.0]])],"derivedFrom":subQ0}),makeQuery(id+"F0.imprint","IMPRINT",EDGE,{"disambiguationData":[TD([[subQ4,1.0]])],"derivedFrom":subQ0}),makeQuery(id+"F0.imprint","IMPRINT",EDGE,{"disambiguationData":[TD([[makeQuery(id+"F0.imprint","INTERSECT",VERTEX,{"derivedFrom":[sQuery(id+"F0.wireOp",EDGE,"E9"),subQ0]}),1.0]])],"derivedFrom":subQ0})])]}),makeQuery(id+"F2.opExtrude","SWEPT_FACE",FACE,{"disambiguationData":[OSD([subQ0]),TDD([makeQuery(id+"F0.imprint","IMPRINT",EDGE,{"disambiguationData":[TD([[makeQuery(id+"F0.imprint","INTERSECT",VERTEX,{"derivedFrom":[sQuery(id+"F0.wireOp",EDGE,"E7"),subQ0]}),-1.0]])],"derivedFrom":subQ0}),makeQuery(id+"F0.imprint","IMPRINT",EDGE,{"disambiguationData":[TD([[subQ1,1.0]])],"derivedFrom":subQ0}),makeQuery(id+"F0.imprint","IMPRINT",EDGE,{"disambiguationData":[TD([[subQ1,-1.0]])],"derivedFrom":subQ0})])]})]})]});}
            var Q16;
            {var subQ0=sQuery(id+"F0.wireOp",EDGE,"E26.trimOffspring");var subQ1=makeQuery(id+"F0.imprint","INTERSECT",VERTEX,{"derivedFrom":[sQuery(id+"F0.wireOp",EDGE,"E11"),subQ0]});var subQ3=sQuery(id+"F0.wireOp",EDGE,"E7");var subQ4=makeQuery(id+"F0.imprint","INTERSECT",VERTEX,{"derivedFrom":[sQuery(id+"F0.wireOp",EDGE,"E14"),subQ0]});var subQ5=makeQuery(id+"F0.imprint","INTERSECT",VERTEX,{"derivedFrom":[sQuery(id+"F0.wireOp",EDGE,"E23.trimOffspring"),subQ0]});Q16=makeQuery(id+"F8.opChamfer","BLEND_EDGE",EDGE,{"blendedFrom":[makeQuery(id+"F2.opExtrude","CAP_EDGE",EDGE,{"disambiguationData":[OSD([subQ3])],"isStart":false}),makeQuery(id+"F2.boolean.opBoolean","MERGE",FACE,{"derivedFrom":[makeQuery(id+"F1.opExtrude","SWEPT_FACE",FACE,{"disambiguationData":[OSD([subQ0])]}),makeQuery(id+"F2.opExtrude","SWEPT_FACE",FACE,{"disambiguationData":[OSD([subQ0]),TDD([makeQuery(id+"F0.imprint","IMPRINT",EDGE,{"disambiguationData":[TD([[subQ5,1.0]])],"derivedFrom":subQ0}),makeQuery(id+"F0.imprint","IMPRINT",EDGE,{"disambiguationData":[TD([[subQ4,1.0]])],"derivedFrom":subQ0}),makeQuery(id+"F0.imprint","IMPRINT",EDGE,{"disambiguationData":[TD([[makeQuery(id+"F0.imprint","INTERSECT",VERTEX,{"derivedFrom":[sQuery(id+"F0.wireOp",EDGE,"E9"),subQ0]}),1.0]])],"derivedFrom":subQ0})])]}),makeQuery(id+"F2.opExtrude","SWEPT_FACE",FACE,{"disambiguationData":[OSD([subQ0]),TDD([makeQuery(id+"F0.imprint","IMPRINT",EDGE,{"disambiguationData":[TD([[makeQuery(id+"F0.imprint","INTERSECT",VERTEX,{"derivedFrom":[subQ3,subQ0]}),-1.0]])],"derivedFrom":subQ0}),makeQuery(id+"F0.imprint","IMPRINT",EDGE,{"disambiguationData":[TD([[subQ1,1.0]])],"derivedFrom":subQ0}),makeQuery(id+"F0.imprint","IMPRINT",EDGE,{"disambiguationData":[TD([[subQ1,-1.0]])],"derivedFrom":subQ0})])]})]})],"blendedInto":[makeQuery(id+"F2.boolean.opBoolean","MERGE",FACE,{"derivedFrom":[makeQuery(id+"F1.opExtrude","SWEPT_FACE",FACE,{"disambiguationData":[OSD([subQ0])]}),makeQuery(id+"F2.opExtrude","SWEPT_FACE",FACE,{"disambiguationData":[OSD([subQ0]),TDD([makeQuery(id+"F0.imprint","IMPRINT",EDGE,{"disambiguationData":[TD([[subQ5,1.0]])],"derivedFrom":subQ0}),makeQuery(id+"F0.imprint","IMPRINT",EDGE,{"disambiguationData":[TD([[subQ4,1.0]])],"derivedFrom":subQ0}),makeQuery(id+"F0.imprint","IMPRINT",EDGE,{"disambiguationData":[TD([[makeQuery(id+"F0.imprint","INTERSECT",VERTEX,{"derivedFrom":[sQuery(id+"F0.wireOp",EDGE,"E9"),subQ0]}),1.0]])],"derivedFrom":subQ0})])]}),makeQuery(id+"F2.opExtrude","SWEPT_FACE",FACE,{"disambiguationData":[OSD([subQ0]),TDD([makeQuery(id+"F0.imprint","IMPRINT",EDGE,{"disambiguationData":[TD([[makeQuery(id+"F0.imprint","INTERSECT",VERTEX,{"derivedFrom":[subQ3,subQ0]}),-1.0]])],"derivedFrom":subQ0}),makeQuery(id+"F0.imprint","IMPRINT",EDGE,{"disambiguationData":[TD([[subQ1,1.0]])],"derivedFrom":subQ0}),makeQuery(id+"F0.imprint","IMPRINT",EDGE,{"disambiguationData":[TD([[subQ1,-1.0]])],"derivedFrom":subQ0})])]})]})]});}
            var Q17;
            {var subQ0=sQuery(id+"F0.wireOp",EDGE,"E27.trimOffspring");var subQ1=makeQuery(id+"F0.imprint","INTERSECT",VERTEX,{"derivedFrom":[sQuery(id+"F0.wireOp",EDGE,"E11"),subQ0]});var subQ3=sQuery(id+"F0.wireOp",EDGE,"E7");var subQ4=makeQuery(id+"F0.imprint","INTERSECT",VERTEX,{"derivedFrom":[sQuery(id+"F0.wireOp",EDGE,"E14"),subQ0]});var subQ5=makeQuery(id+"F0.imprint","INTERSECT",VERTEX,{"derivedFrom":[sQuery(id+"F0.wireOp",EDGE,"E23.trimOffspring"),subQ0]});Q17=makeQuery(id+"F8.opChamfer","BLEND_EDGE",EDGE,{"blendedFrom":[makeQuery(id+"F2.opExtrude","CAP_EDGE",EDGE,{"disambiguationData":[OSD([subQ3])],"isStart":false}),makeQuery(id+"F2.boolean.opBoolean","MERGE",FACE,{"derivedFrom":[makeQuery(id+"F1.opExtrude","SWEPT_FACE",FACE,{"disambiguationData":[OSD([subQ0])]}),makeQuery(id+"F2.opExtrude","SWEPT_FACE",FACE,{"disambiguationData":[OSD([subQ0]),TDD([makeQuery(id+"F0.imprint","IMPRINT",EDGE,{"disambiguationData":[TD([[subQ5,1.0]])],"derivedFrom":subQ0}),makeQuery(id+"F0.imprint","IMPRINT",EDGE,{"disambiguationData":[TD([[subQ4,1.0]])],"derivedFrom":subQ0}),makeQuery(id+"F0.imprint","IMPRINT",EDGE,{"disambiguationData":[TD([[makeQuery(id+"F0.imprint","INTERSECT",VERTEX,{"derivedFrom":[sQuery(id+"F0.wireOp",EDGE,"E9"),subQ0]}),1.0]])],"derivedFrom":subQ0})])]}),makeQuery(id+"F2.opExtrude","SWEPT_FACE",FACE,{"disambiguationData":[OSD([subQ0]),TDD([makeQuery(id+"F0.imprint","IMPRINT",EDGE,{"disambiguationData":[TD([[makeQuery(id+"F0.imprint","INTERSECT",VERTEX,{"derivedFrom":[subQ3,subQ0]}),-1.0]])],"derivedFrom":subQ0}),makeQuery(id+"F0.imprint","IMPRINT",EDGE,{"disambiguationData":[TD([[subQ1,1.0]])],"derivedFrom":subQ0}),makeQuery(id+"F0.imprint","IMPRINT",EDGE,{"disambiguationData":[TD([[subQ1,-1.0]])],"derivedFrom":subQ0})])]})]})],"blendedInto":[makeQuery(id+"F2.boolean.opBoolean","MERGE",FACE,{"derivedFrom":[makeQuery(id+"F1.opExtrude","SWEPT_FACE",FACE,{"disambiguationData":[OSD([subQ0])]}),makeQuery(id+"F2.opExtrude","SWEPT_FACE",FACE,{"disambiguationData":[OSD([subQ0]),TDD([makeQuery(id+"F0.imprint","IMPRINT",EDGE,{"disambiguationData":[TD([[subQ5,1.0]])],"derivedFrom":subQ0}),makeQuery(id+"F0.imprint","IMPRINT",EDGE,{"disambiguationData":[TD([[subQ4,1.0]])],"derivedFrom":subQ0}),makeQuery(id+"F0.imprint","IMPRINT",EDGE,{"disambiguationData":[TD([[makeQuery(id+"F0.imprint","INTERSECT",VERTEX,{"derivedFrom":[sQuery(id+"F0.wireOp",EDGE,"E9"),subQ0]}),1.0]])],"derivedFrom":subQ0})])]}),makeQuery(id+"F2.opExtrude","SWEPT_FACE",FACE,{"disambiguationData":[OSD([subQ0]),TDD([makeQuery(id+"F0.imprint","IMPRINT",EDGE,{"disambiguationData":[TD([[makeQuery(id+"F0.imprint","INTERSECT",VERTEX,{"derivedFrom":[subQ3,subQ0]}),-1.0]])],"derivedFrom":subQ0}),makeQuery(id+"F0.imprint","IMPRINT",EDGE,{"disambiguationData":[TD([[subQ1,1.0]])],"derivedFrom":subQ0}),makeQuery(id+"F0.imprint","IMPRINT",EDGE,{"disambiguationData":[TD([[subQ1,-1.0]])],"derivedFrom":subQ0})])]})]})]});}
            var Q18;
            {var subQ0=sQuery(id+"F0.wireOp",EDGE,"E26.trimOffspring");var subQ1=makeQuery(id+"F0.imprint","INTERSECT",VERTEX,{"derivedFrom":[sQuery(id+"F0.wireOp",EDGE,"E11"),subQ0]});var subQ3=sQuery(id+"F0.wireOp",EDGE,"E9");var subQ4=makeQuery(id+"F0.imprint","INTERSECT",VERTEX,{"derivedFrom":[sQuery(id+"F0.wireOp",EDGE,"E14"),subQ0]});var subQ5=makeQuery(id+"F0.imprint","INTERSECT",VERTEX,{"derivedFrom":[sQuery(id+"F0.wireOp",EDGE,"E23.trimOffspring"),subQ0]});Q18=makeQuery(id+"F8.opChamfer","BLEND_EDGE",EDGE,{"blendedFrom":[makeQuery(id+"F2.opExtrude","CAP_EDGE",EDGE,{"disambiguationData":[OSD([subQ3])],"isStart":false}),makeQuery(id+"F2.boolean.opBoolean","MERGE",FACE,{"derivedFrom":[makeQuery(id+"F1.opExtrude","SWEPT_FACE",FACE,{"disambiguationData":[OSD([subQ0])]}),makeQuery(id+"F2.opExtrude","SWEPT_FACE",FACE,{"disambiguationData":[OSD([subQ0]),TDD([makeQuery(id+"F0.imprint","IMPRINT",EDGE,{"disambiguationData":[TD([[subQ5,1.0]])],"derivedFrom":subQ0}),makeQuery(id+"F0.imprint","IMPRINT",EDGE,{"disambiguationData":[TD([[subQ4,1.0]])],"derivedFrom":subQ0}),makeQuery(id+"F0.imprint","IMPRINT",EDGE,{"disambiguationData":[TD([[makeQuery(id+"F0.imprint","INTERSECT",VERTEX,{"derivedFrom":[subQ3,subQ0]}),1.0]])],"derivedFrom":subQ0})])]}),makeQuery(id+"F2.opExtrude","SWEPT_FACE",FACE,{"disambiguationData":[OSD([subQ0]),TDD([makeQuery(id+"F0.imprint","IMPRINT",EDGE,{"disambiguationData":[TD([[makeQuery(id+"F0.imprint","INTERSECT",VERTEX,{"derivedFrom":[sQuery(id+"F0.wireOp",EDGE,"E7"),subQ0]}),-1.0]])],"derivedFrom":subQ0}),makeQuery(id+"F0.imprint","IMPRINT",EDGE,{"disambiguationData":[TD([[subQ1,1.0]])],"derivedFrom":subQ0}),makeQuery(id+"F0.imprint","IMPRINT",EDGE,{"disambiguationData":[TD([[subQ1,-1.0]])],"derivedFrom":subQ0})])]})]})],"blendedInto":[makeQuery(id+"F2.boolean.opBoolean","MERGE",FACE,{"derivedFrom":[makeQuery(id+"F1.opExtrude","SWEPT_FACE",FACE,{"disambiguationData":[OSD([subQ0])]}),makeQuery(id+"F2.opExtrude","SWEPT_FACE",FACE,{"disambiguationData":[OSD([subQ0]),TDD([makeQuery(id+"F0.imprint","IMPRINT",EDGE,{"disambiguationData":[TD([[subQ5,1.0]])],"derivedFrom":subQ0}),makeQuery(id+"F0.imprint","IMPRINT",EDGE,{"disambiguationData":[TD([[subQ4,1.0]])],"derivedFrom":subQ0}),makeQuery(id+"F0.imprint","IMPRINT",EDGE,{"disambiguationData":[TD([[makeQuery(id+"F0.imprint","INTERSECT",VERTEX,{"derivedFrom":[subQ3,subQ0]}),1.0]])],"derivedFrom":subQ0})])]}),makeQuery(id+"F2.opExtrude","SWEPT_FACE",FACE,{"disambiguationData":[OSD([subQ0]),TDD([makeQuery(id+"F0.imprint","IMPRINT",EDGE,{"disambiguationData":[TD([[makeQuery(id+"F0.imprint","INTERSECT",VERTEX,{"derivedFrom":[sQuery(id+"F0.wireOp",EDGE,"E7"),subQ0]}),-1.0]])],"derivedFrom":subQ0}),makeQuery(id+"F0.imprint","IMPRINT",EDGE,{"disambiguationData":[TD([[subQ1,1.0]])],"derivedFrom":subQ0}),makeQuery(id+"F0.imprint","IMPRINT",EDGE,{"disambiguationData":[TD([[subQ1,-1.0]])],"derivedFrom":subQ0})])]})]})]});}
            var Q19;
            {var subQ0=sQuery(id+"F0.wireOp",EDGE,"E27.trimOffspring");var subQ1=makeQuery(id+"F0.imprint","INTERSECT",VERTEX,{"derivedFrom":[sQuery(id+"F0.wireOp",EDGE,"E11"),subQ0]});var subQ3=sQuery(id+"F0.wireOp",EDGE,"E9");var subQ4=makeQuery(id+"F0.imprint","INTERSECT",VERTEX,{"derivedFrom":[sQuery(id+"F0.wireOp",EDGE,"E14"),subQ0]});var subQ5=makeQuery(id+"F0.imprint","INTERSECT",VERTEX,{"derivedFrom":[sQuery(id+"F0.wireOp",EDGE,"E23.trimOffspring"),subQ0]});Q19=makeQuery(id+"F8.opChamfer","BLEND_EDGE",EDGE,{"blendedFrom":[makeQuery(id+"F2.opExtrude","CAP_EDGE",EDGE,{"disambiguationData":[OSD([subQ3])],"isStart":false}),makeQuery(id+"F2.boolean.opBoolean","MERGE",FACE,{"derivedFrom":[makeQuery(id+"F1.opExtrude","SWEPT_FACE",FACE,{"disambiguationData":[OSD([subQ0])]}),makeQuery(id+"F2.opExtrude","SWEPT_FACE",FACE,{"disambiguationData":[OSD([subQ0]),TDD([makeQuery(id+"F0.imprint","IMPRINT",EDGE,{"disambiguationData":[TD([[subQ5,1.0]])],"derivedFrom":subQ0}),makeQuery(id+"F0.imprint","IMPRINT",EDGE,{"disambiguationData":[TD([[subQ4,1.0]])],"derivedFrom":subQ0}),makeQuery(id+"F0.imprint","IMPRINT",EDGE,{"disambiguationData":[TD([[makeQuery(id+"F0.imprint","INTERSECT",VERTEX,{"derivedFrom":[subQ3,subQ0]}),1.0]])],"derivedFrom":subQ0})])]}),makeQuery(id+"F2.opExtrude","SWEPT_FACE",FACE,{"disambiguationData":[OSD([subQ0]),TDD([makeQuery(id+"F0.imprint","IMPRINT",EDGE,{"disambiguationData":[TD([[makeQuery(id+"F0.imprint","INTERSECT",VERTEX,{"derivedFrom":[sQuery(id+"F0.wireOp",EDGE,"E7"),subQ0]}),-1.0]])],"derivedFrom":subQ0}),makeQuery(id+"F0.imprint","IMPRINT",EDGE,{"disambiguationData":[TD([[subQ1,1.0]])],"derivedFrom":subQ0}),makeQuery(id+"F0.imprint","IMPRINT",EDGE,{"disambiguationData":[TD([[subQ1,-1.0]])],"derivedFrom":subQ0})])]})]})],"blendedInto":[makeQuery(id+"F2.boolean.opBoolean","MERGE",FACE,{"derivedFrom":[makeQuery(id+"F1.opExtrude","SWEPT_FACE",FACE,{"disambiguationData":[OSD([subQ0])]}),makeQuery(id+"F2.opExtrude","SWEPT_FACE",FACE,{"disambiguationData":[OSD([subQ0]),TDD([makeQuery(id+"F0.imprint","IMPRINT",EDGE,{"disambiguationData":[TD([[subQ5,1.0]])],"derivedFrom":subQ0}),makeQuery(id+"F0.imprint","IMPRINT",EDGE,{"disambiguationData":[TD([[subQ4,1.0]])],"derivedFrom":subQ0}),makeQuery(id+"F0.imprint","IMPRINT",EDGE,{"disambiguationData":[TD([[makeQuery(id+"F0.imprint","INTERSECT",VERTEX,{"derivedFrom":[subQ3,subQ0]}),1.0]])],"derivedFrom":subQ0})])]}),makeQuery(id+"F2.opExtrude","SWEPT_FACE",FACE,{"disambiguationData":[OSD([subQ0]),TDD([makeQuery(id+"F0.imprint","IMPRINT",EDGE,{"disambiguationData":[TD([[makeQuery(id+"F0.imprint","INTERSECT",VERTEX,{"derivedFrom":[sQuery(id+"F0.wireOp",EDGE,"E7"),subQ0]}),-1.0]])],"derivedFrom":subQ0}),makeQuery(id+"F0.imprint","IMPRINT",EDGE,{"disambiguationData":[TD([[subQ1,1.0]])],"derivedFrom":subQ0}),makeQuery(id+"F0.imprint","IMPRINT",EDGE,{"disambiguationData":[TD([[subQ1,-1.0]])],"derivedFrom":subQ0})])]})]})]});}
            var Q20;
            {var subQ0=sQuery(id+"F0.wireOp",EDGE,"E26.trimOffspring");var subQ1=makeQuery(id+"F0.imprint","INTERSECT",VERTEX,{"derivedFrom":[sQuery(id+"F0.wireOp",EDGE,"E11"),subQ0]});var subQ3=makeQuery(id+"F0.imprint","INTERSECT",VERTEX,{"derivedFrom":[sQuery(id+"F0.wireOp",EDGE,"E14"),subQ0]});var subQ4=makeQuery(id+"F0.imprint","INTERSECT",VERTEX,{"derivedFrom":[sQuery(id+"F0.wireOp",EDGE,"E23.trimOffspring"),subQ0]});var subQ5=sQuery(id+"F0.wireOp",EDGE,"E24.trimOffspring");Q20=makeQuery(id+"F8.opChamfer","BLEND_EDGE",EDGE,{"blendedFrom":[makeQuery(id+"F2.opExtrude","CAP_EDGE",EDGE,{"disambiguationData":[OSD([subQ5])],"isStart":false}),makeQuery(id+"F2.boolean.opBoolean","MERGE",FACE,{"derivedFrom":[makeQuery(id+"F1.opExtrude","SWEPT_FACE",FACE,{"disambiguationData":[OSD([subQ0])]}),makeQuery(id+"F2.opExtrude","SWEPT_FACE",FACE,{"disambiguationData":[OSD([subQ0]),TDD([makeQuery(id+"F0.imprint","IMPRINT",EDGE,{"disambiguationData":[TD([[subQ4,1.0]])],"derivedFrom":subQ0}),makeQuery(id+"F0.imprint","IMPRINT",EDGE,{"disambiguationData":[TD([[subQ3,1.0]])],"derivedFrom":subQ0}),makeQuery(id+"F0.imprint","IMPRINT",EDGE,{"disambiguationData":[TD([[makeQuery(id+"F0.imprint","INTERSECT",VERTEX,{"derivedFrom":[sQuery(id+"F0.wireOp",EDGE,"E9"),subQ0]}),1.0]])],"derivedFrom":subQ0})])]}),makeQuery(id+"F2.opExtrude","SWEPT_FACE",FACE,{"disambiguationData":[OSD([subQ0]),TDD([makeQuery(id+"F0.imprint","IMPRINT",EDGE,{"disambiguationData":[TD([[makeQuery(id+"F0.imprint","INTERSECT",VERTEX,{"derivedFrom":[sQuery(id+"F0.wireOp",EDGE,"E7"),subQ0]}),-1.0]])],"derivedFrom":subQ0}),makeQuery(id+"F0.imprint","IMPRINT",EDGE,{"disambiguationData":[TD([[subQ1,1.0]])],"derivedFrom":subQ0}),makeQuery(id+"F0.imprint","IMPRINT",EDGE,{"disambiguationData":[TD([[subQ1,-1.0]])],"derivedFrom":subQ0})])]})]})],"blendedInto":[makeQuery(id+"F2.boolean.opBoolean","MERGE",FACE,{"derivedFrom":[makeQuery(id+"F1.opExtrude","SWEPT_FACE",FACE,{"disambiguationData":[OSD([subQ0])]}),makeQuery(id+"F2.opExtrude","SWEPT_FACE",FACE,{"disambiguationData":[OSD([subQ0]),TDD([makeQuery(id+"F0.imprint","IMPRINT",EDGE,{"disambiguationData":[TD([[subQ4,1.0]])],"derivedFrom":subQ0}),makeQuery(id+"F0.imprint","IMPRINT",EDGE,{"disambiguationData":[TD([[subQ3,1.0]])],"derivedFrom":subQ0}),makeQuery(id+"F0.imprint","IMPRINT",EDGE,{"disambiguationData":[TD([[makeQuery(id+"F0.imprint","INTERSECT",VERTEX,{"derivedFrom":[sQuery(id+"F0.wireOp",EDGE,"E9"),subQ0]}),1.0]])],"derivedFrom":subQ0})])]}),makeQuery(id+"F2.opExtrude","SWEPT_FACE",FACE,{"disambiguationData":[OSD([subQ0]),TDD([makeQuery(id+"F0.imprint","IMPRINT",EDGE,{"disambiguationData":[TD([[makeQuery(id+"F0.imprint","INTERSECT",VERTEX,{"derivedFrom":[sQuery(id+"F0.wireOp",EDGE,"E7"),subQ0]}),-1.0]])],"derivedFrom":subQ0}),makeQuery(id+"F0.imprint","IMPRINT",EDGE,{"disambiguationData":[TD([[subQ1,1.0]])],"derivedFrom":subQ0}),makeQuery(id+"F0.imprint","IMPRINT",EDGE,{"disambiguationData":[TD([[subQ1,-1.0]])],"derivedFrom":subQ0})])]})]})]});}
            var Q21;
            {var subQ0=sQuery(id+"F0.wireOp",EDGE,"E27.trimOffspring");var subQ1=makeQuery(id+"F0.imprint","INTERSECT",VERTEX,{"derivedFrom":[sQuery(id+"F0.wireOp",EDGE,"E11"),subQ0]});var subQ3=makeQuery(id+"F0.imprint","INTERSECT",VERTEX,{"derivedFrom":[sQuery(id+"F0.wireOp",EDGE,"E14"),subQ0]});var subQ4=makeQuery(id+"F0.imprint","INTERSECT",VERTEX,{"derivedFrom":[sQuery(id+"F0.wireOp",EDGE,"E23.trimOffspring"),subQ0]});var subQ5=sQuery(id+"F0.wireOp",EDGE,"E24.trimOffspring");Q21=makeQuery(id+"F8.opChamfer","BLEND_EDGE",EDGE,{"blendedFrom":[makeQuery(id+"F2.opExtrude","CAP_EDGE",EDGE,{"disambiguationData":[OSD([subQ5])],"isStart":false}),makeQuery(id+"F2.boolean.opBoolean","MERGE",FACE,{"derivedFrom":[makeQuery(id+"F1.opExtrude","SWEPT_FACE",FACE,{"disambiguationData":[OSD([subQ0])]}),makeQuery(id+"F2.opExtrude","SWEPT_FACE",FACE,{"disambiguationData":[OSD([subQ0]),TDD([makeQuery(id+"F0.imprint","IMPRINT",EDGE,{"disambiguationData":[TD([[subQ4,1.0]])],"derivedFrom":subQ0}),makeQuery(id+"F0.imprint","IMPRINT",EDGE,{"disambiguationData":[TD([[subQ3,1.0]])],"derivedFrom":subQ0}),makeQuery(id+"F0.imprint","IMPRINT",EDGE,{"disambiguationData":[TD([[makeQuery(id+"F0.imprint","INTERSECT",VERTEX,{"derivedFrom":[sQuery(id+"F0.wireOp",EDGE,"E9"),subQ0]}),1.0]])],"derivedFrom":subQ0})])]}),makeQuery(id+"F2.opExtrude","SWEPT_FACE",FACE,{"disambiguationData":[OSD([subQ0]),TDD([makeQuery(id+"F0.imprint","IMPRINT",EDGE,{"disambiguationData":[TD([[makeQuery(id+"F0.imprint","INTERSECT",VERTEX,{"derivedFrom":[sQuery(id+"F0.wireOp",EDGE,"E7"),subQ0]}),-1.0]])],"derivedFrom":subQ0}),makeQuery(id+"F0.imprint","IMPRINT",EDGE,{"disambiguationData":[TD([[subQ1,1.0]])],"derivedFrom":subQ0}),makeQuery(id+"F0.imprint","IMPRINT",EDGE,{"disambiguationData":[TD([[subQ1,-1.0]])],"derivedFrom":subQ0})])]})]})],"blendedInto":[makeQuery(id+"F2.boolean.opBoolean","MERGE",FACE,{"derivedFrom":[makeQuery(id+"F1.opExtrude","SWEPT_FACE",FACE,{"disambiguationData":[OSD([subQ0])]}),makeQuery(id+"F2.opExtrude","SWEPT_FACE",FACE,{"disambiguationData":[OSD([subQ0]),TDD([makeQuery(id+"F0.imprint","IMPRINT",EDGE,{"disambiguationData":[TD([[subQ4,1.0]])],"derivedFrom":subQ0}),makeQuery(id+"F0.imprint","IMPRINT",EDGE,{"disambiguationData":[TD([[subQ3,1.0]])],"derivedFrom":subQ0}),makeQuery(id+"F0.imprint","IMPRINT",EDGE,{"disambiguationData":[TD([[makeQuery(id+"F0.imprint","INTERSECT",VERTEX,{"derivedFrom":[sQuery(id+"F0.wireOp",EDGE,"E9"),subQ0]}),1.0]])],"derivedFrom":subQ0})])]}),makeQuery(id+"F2.opExtrude","SWEPT_FACE",FACE,{"disambiguationData":[OSD([subQ0]),TDD([makeQuery(id+"F0.imprint","IMPRINT",EDGE,{"disambiguationData":[TD([[makeQuery(id+"F0.imprint","INTERSECT",VERTEX,{"derivedFrom":[sQuery(id+"F0.wireOp",EDGE,"E7"),subQ0]}),-1.0]])],"derivedFrom":subQ0}),makeQuery(id+"F0.imprint","IMPRINT",EDGE,{"disambiguationData":[TD([[subQ1,1.0]])],"derivedFrom":subQ0}),makeQuery(id+"F0.imprint","IMPRINT",EDGE,{"disambiguationData":[TD([[subQ1,-1.0]])],"derivedFrom":subQ0})])]})]})]});}
            fillet(context, id + "F10", {"entities" : qUnion([Q0, Q1, Q2, Q3, Q4, Q5, Q6, Q7, Q8, Q9, Q10, Q11, Q12, Q13, Q14, Q15, Q16, Q17, Q18, Q19, Q20, Q21]), "radius" : 2 * mm, "tangentPropagation" : true, "allowEdgeOverflow" : false});
        }
    });
